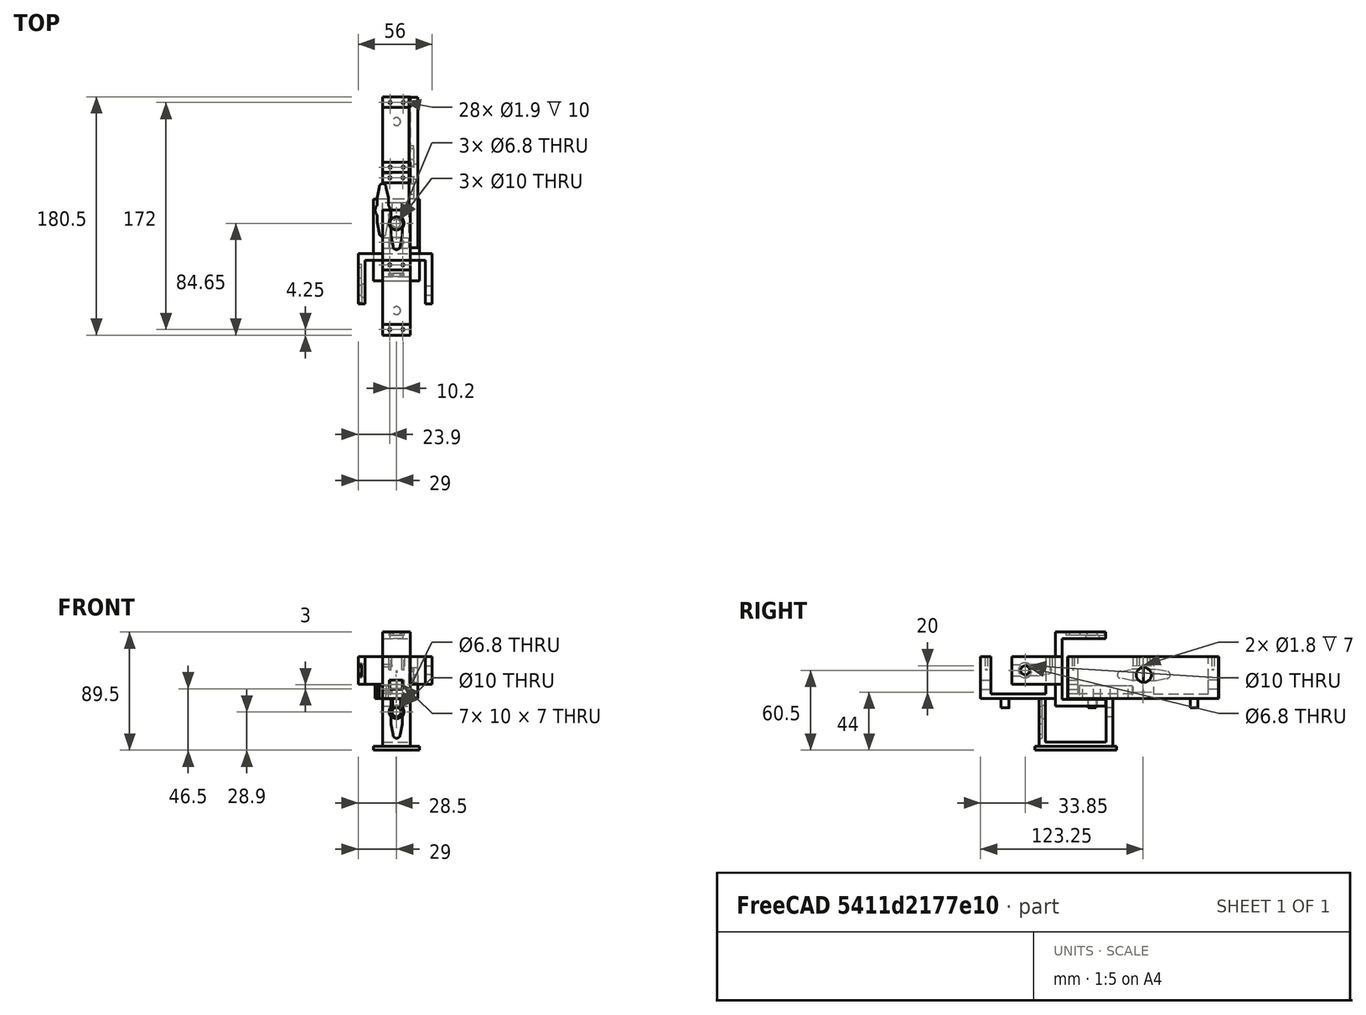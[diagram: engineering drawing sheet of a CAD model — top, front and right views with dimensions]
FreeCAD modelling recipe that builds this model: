
FCSTD DOCUMENT  (FreeCAD 1.0R39109 (Git))
Label: Piernas
License: All rights reserved
LicenseURL: https://en.wikipedia.org/wiki/All_rights_reserved
objects: Part::Cylinder×46, Part::MultiFuse×39, Part::Cut×27, Sketcher::SketchObject×21, PartDesign::Pad×21, PartDesign::Body×21, Part::Box×9, App::DocumentObjectGroup×8, Spreadsheet::Sheet×1, Mesh::Feature×1
note: 247 computed .brp shape members not serialized (recipe doc carries the construction recipe); baked Part::Feature solids carry a one-line shape summary decoded from their .brp

FEATURE [Sketcher::SketchObject] Sketch
  ArcFitTolerance = 0
  AttachmentSupport = -> [YZ_Plane]
  FullyConstrained = true
  MakeInternals = false
  MapMode = 5
  Placement = pos=(0,0,0) rot=(0.57735,0.57735,0.57735;2.0944rad)
  expr: Constraints[10] = Spreadsheet.H_Largo
  expr: Constraints[12] = Spreadsheet.H_BaseAlto
  expr: Constraints[13] = Spreadsheet.H_AltoServo
  expr: Constraints[14] = Spreadsheet.H_AnchoAgg
  sketch-geometry (8):
    g0: LineSegment StartX=-28.75 StartY=32 StartZ=0 EndX=-28.75 EndY=0 EndZ=0
    g1: LineSegment StartX=-28.75 StartY=0 StartZ=0 EndX=28.75 EndY=0 EndZ=0
    g2: LineSegment StartX=28.75 StartY=0 StartZ=0 EndX=28.75 EndY=32 EndZ=0
    g3: LineSegment StartX=28.75 StartY=32 StartZ=0 EndX=20.75 EndY=32 EndZ=0
    g4: LineSegment StartX=20.75 StartY=32 StartZ=0 EndX=20.75 EndY=3.5 EndZ=0
    g5: LineSegment StartX=20.75 StartY=3.5 StartZ=0 EndX=-20.75 EndY=3.5 EndZ=0
    g6: LineSegment StartX=-20.75 StartY=3.5 StartZ=0 EndX=-20.75 EndY=32 EndZ=0
    g7: LineSegment StartX=-28.75 StartY=32 StartZ=0 EndX=-20.75 EndY=32 EndZ=0
  constraints (21):
    c: Coincident(g1,g0)
    c: Coincident(g2,g1)
    c: Vertical(g2)
    c: Coincident(g3,g2)
    c: Coincident(g4,g3)
    c: Vertical(g4)
    c: Coincident(g5,g4)
    c: Horizontal(g5)
    c: Coincident(g6,g5)
    c: Vertical(g6)
    c: DistanceX(g5,g5) = 41.5
    c: Symmetric(g6,g3,g-2)
    c: DistanceY(g0,g5) = 3.5
    c: DistanceY(g4,g4) = 28.5
    c: DistanceX(g3,g3) = 8
    c: Symmetric(g1,g0,g-2)
    c: Symmetric(g0,g2,g-2)
    c: Coincident(g7,g0)
    c: Coincident(g7,g6)
    c: Horizontal(g7)
    c: PointOnObject(g0,g-1)
FEATURE [Spreadsheet::Sheet] Spreadsheet
  cells = A1='HOLDER SERVO; D1='UNION SERVOS; G1='PIE; A2='largo; B2(H_Largo)=41.5; D2='separacion entre servos; E2(U_sepa)=0.5; G2='Largo; H2(P_largo)=62; A3='BaseAlto; B3(H_BaseAlto)=3.5; D3='Grosor Paredes; E3(U_Grosor)=5; G3='Ancho; H3(P_acnho)=35; A4='Alto Servo; B4(H_AltoServo)=28.5; D4='LargoMedio-Sal; E4(U_LargoM)=33; A5='Ancho Aggraderas; B5(H_AnchoAgg)=8; D5='AltoBase-Techo; E5(U_AltoB)=45.5; A6='Ancho Base; B6(H_AnchoBase)=21; A7='Distanciatonillos; B7(H_DistanciaTornillos)=8; A8='RadioTornillos; B8(H_RadioTornillos)==2.3 / 2 - 0.2; A9='Radio eje; B9(H_RadioEje)=3
FEATURE [PartDesign::Pad] Pad
  Direction = (1,-2e-16,3e-16)
  Length = 21
  Length2 = 10
  Placement = pos=(0,0,0) rot=(0.57735,0.57735,0.57735;2.0944rad)
  Profile = -> Sketch
  ReferenceAxis = -> Sketch [N_Axis]
  Suppressed = false
  Type = 0
  expr: Length = Spreadsheet.H_AnchoBase
FEATURE [PartDesign::Body] Body  label="ServoHolder"
  AllowCompound = false
  Group = -> [Sketch,Pad]
  Origin = -> Origin
  Tip = -> Pad
FEATURE [Part::Box] Box  label="Cube"
  AttacherType = Attacher::AttachEngine3D
  Height = 7
  Length = 10
  Placement = pos=(5,-29,4) rot=(0,0,1;0rad)
  Width = 10
FEATURE [Part::Cut] Cut
  Base = -> Body
  Tool = -> Box
FEATURE [Part::Cylinder] Cylinder
  Angle = 360
  AttacherType = Attacher::AttachEngine3D
  FirstAngle = 0
  Height = 10
  Placement = pos=(9.9,0,0) rot=(0,0,1;0rad)
  Radius = 0.95
  SecondAngle = 0
  expr: .Placement.Base.x = Spreadsheet.H_RadioTornillos * 2 + Spreadsheet.H_DistanciaTornillos
  expr: Radius = Spreadsheet.H_RadioTornillos
FEATURE [Part::Cylinder] Cylinder001
  Angle = 360
  AttacherType = Attacher::AttachEngine3D
  FirstAngle = 0
  Height = 10
  Radius = 0.95
  SecondAngle = 0
  expr: Radius = Spreadsheet.H_RadioTornillos
FEATURE [Part::MultiFuse] Fusion  label="Tornillos"
  Placement = pos=(5,24.5,22) rot=(0,0,1;0rad)
  Shapes = -> [Cylinder001,Cylinder]
FEATURE [Part::Cylinder] Cylinder002
  Angle = 360
  AttacherType = Attacher::AttachEngine3D
  FirstAngle = 0
  Height = 10
  Placement = pos=(9.9,0,0) rot=(0,0,1;0rad)
  Radius = 0.95
  SecondAngle = 0
  expr: .Placement.Base.x = Spreadsheet.H_RadioTornillos * 2 + Spreadsheet.H_DistanciaTornillos
  expr: Radius = Spreadsheet.H_RadioTornillos
FEATURE [Part::Cylinder] Cylinder003
  Angle = 360
  AttacherType = Attacher::AttachEngine3D
  FirstAngle = 0
  Height = 10
  Radius = 0.95
  SecondAngle = 0
  expr: Radius = Spreadsheet.H_RadioTornillos
FEATURE [Part::MultiFuse] Fusion001  label="Tornillos001"
  Placement = pos=(5,-24.5,22) rot=(0,0,1;0rad)
  Shapes = -> [Cylinder003,Cylinder002]
FEATURE [Part::MultiFuse] Fusion002
  Placement = pos=(0.4,0,0) rot=(0,0,1;0rad)
  Shapes = -> [Fusion,Fusion001]
FEATURE [Part::Cut] Cut001  label="Holder001"
  Base = -> Cut
  Tool = -> Fusion002
FEATURE [Part::Cylinder] Cylinder012
  Angle = 360
  AttacherType = Attacher::AttachEngine3D
  FirstAngle = 0
  Height = 10
  Placement = pos=(10.5,-10.1,-7) rot=(0,0,1;0rad)
  Radius = 3
  SecondAngle = 0
  expr: Radius = Spreadsheet.H_RadioEje
FEATURE [Part::Box] Box003  label="Cube003"
  AttacherType = Attacher::AttachEngine3D
  Height = 7
  Length = 10
  Placement = pos=(5,-29,7) rot=(0,0,1;0rad)
  Width = 10
FEATURE [Part::Cylinder] Cylinder013
  Angle = 360
  AttacherType = Attacher::AttachEngine3D
  FirstAngle = 0
  Height = 10
  Placement = pos=(9.9,0,0) rot=(0,0,1;0rad)
  Radius = 0.95
  SecondAngle = 0
  expr: .Placement.Base.x = Spreadsheet.H_RadioTornillos * 2 + Spreadsheet.H_DistanciaTornillos
  expr: Radius = Spreadsheet.H_RadioTornillos
FEATURE [Part::Cylinder] Cylinder014
  Angle = 360
  AttacherType = Attacher::AttachEngine3D
  FirstAngle = 0
  Height = 10
  Radius = 0.95
  SecondAngle = 0
  expr: Radius = Spreadsheet.H_RadioTornillos
FEATURE [Part::Cylinder] Cylinder015
  Angle = 360
  AttacherType = Attacher::AttachEngine3D
  FirstAngle = 0
  Height = 10
  Placement = pos=(9.9,0,0) rot=(0,0,1;0rad)
  Radius = 0.95
  SecondAngle = 0
  expr: .Placement.Base.x = Spreadsheet.H_RadioTornillos * 2 + Spreadsheet.H_DistanciaTornillos
  expr: Radius = Spreadsheet.H_RadioTornillos
FEATURE [Part::Cylinder] Cylinder016
  Angle = 360
  AttacherType = Attacher::AttachEngine3D
  FirstAngle = 0
  Height = 10
  Radius = 0.95
  SecondAngle = 0
  expr: Radius = Spreadsheet.H_RadioTornillos
FEATURE [Part::MultiFuse] Fusion010  label="Tornillos006"
  Placement = pos=(5,24.5,22) rot=(0,0,1;0rad)
  Shapes = -> [Cylinder014,Cylinder013]
FEATURE [Part::MultiFuse] Fusion011  label="Tornillos007"
  Placement = pos=(5,-24.5,22) rot=(0,0,1;0rad)
  Shapes = -> [Cylinder016,Cylinder015]
FEATURE [Part::MultiFuse] Fusion012
  Placement = pos=(0.4,0,0) rot=(0,0,1;0rad)
  Shapes = -> [Fusion010,Fusion011]
FEATURE [Sketcher::SketchObject] Sketch003
  ArcFitTolerance = 0
  AttachmentSupport = -> [YZ_Plane003]
  FullyConstrained = true
  MakeInternals = false
  MapMode = 5
  Placement = pos=(0,0,0) rot=(0.57735,0.57735,0.57735;2.0944rad)
  expr: Constraints[10] = Spreadsheet.H_Largo
  expr: Constraints[12] = Spreadsheet.H_BaseAlto
  expr: Constraints[13] = Spreadsheet.H_AltoServo
  expr: Constraints[14] = Spreadsheet.H_AnchoAgg
  sketch-geometry (8):
    g0: LineSegment StartX=-28.75 StartY=32 StartZ=0 EndX=-28.75 EndY=0 EndZ=0
    g1: LineSegment StartX=-28.75 StartY=0 StartZ=0 EndX=28.75 EndY=0 EndZ=0
    g2: LineSegment StartX=28.75 StartY=0 StartZ=0 EndX=28.75 EndY=32 EndZ=0
    g3: LineSegment StartX=28.75 StartY=32 StartZ=0 EndX=20.75 EndY=32 EndZ=0
    g4: LineSegment StartX=20.75 StartY=32 StartZ=0 EndX=20.75 EndY=3.5 EndZ=0
    g5: LineSegment StartX=20.75 StartY=3.5 StartZ=0 EndX=-20.75 EndY=3.5 EndZ=0
    g6: LineSegment StartX=-20.75 StartY=3.5 StartZ=0 EndX=-20.75 EndY=32 EndZ=0
    g7: LineSegment StartX=-28.75 StartY=32 StartZ=0 EndX=-20.75 EndY=32 EndZ=0
  constraints (21):
    c: Coincident(g1,g0)
    c: Coincident(g2,g1)
    c: Vertical(g2)
    c: Coincident(g3,g2)
    c: Coincident(g4,g3)
    c: Vertical(g4)
    c: Coincident(g5,g4)
    c: Horizontal(g5)
    c: Coincident(g6,g5)
    c: Vertical(g6)
    c: DistanceX(g5,g5) = 41.5
    c: Symmetric(g6,g3,g-2)
    c: DistanceY(g0,g5) = 3.5
    c: DistanceY(g4,g4) = 28.5
    c: DistanceX(g3,g3) = 8
    c: Symmetric(g1,g0,g-2)
    c: Symmetric(g0,g2,g-2)
    c: Coincident(g7,g0)
    c: Coincident(g7,g6)
    c: Horizontal(g7)
    c: PointOnObject(g0,g-1)
FEATURE [PartDesign::Pad] Pad003
  Direction = (1,-2e-16,3e-16)
  Length = 21
  Length2 = 10
  Placement = pos=(0,0,0) rot=(0.57735,0.57735,0.57735;2.0944rad)
  Profile = -> Sketch003
  ReferenceAxis = -> Sketch003 [N_Axis]
  Suppressed = false
  Type = 0
  expr: Length = Spreadsheet.H_AnchoBase
FEATURE [PartDesign::Body] Body003  label="ServoHolder003"
  AllowCompound = false
  Group = -> [Sketch003,Pad003]
  Origin = -> Origin003
  Tip = -> Pad003
FEATURE [Part::Cut] Cut006
  Base = -> Body003
  Tool = -> Box003
FEATURE [Part::Cut] Cut007  label="Holder004"
  Base = -> Cut006
  Tool = -> Fusion012
FEATURE [Part::MultiFuse] Fusion013  label="HolderCEje"
  Shapes = -> [Cylinder012,Cut007]
FEATURE [App::DocumentObjectGroup] Group  label="Muslo2"
  Group = -> [Cut001,Fusion013]
FEATURE [Sketcher::SketchObject] Sketch004
  ArcFitTolerance = 0
  AttachmentSupport = -> [YZ_Plane004]
  FullyConstrained = true
  MakeInternals = false
  MapMode = 5
  Placement = pos=(0,0,0) rot=(0.57735,0.57735,0.57735;2.0944rad)
  expr: Constraints[16] = Spreadsheet.U_sepa
  expr: Constraints[17] = Spreadsheet.U_LargoM
  expr: Constraints[20] = Spreadsheet.U_Grosor
  expr: Constraints[21] = Spreadsheet.U_Grosor
  expr: Constraints[22] = Spreadsheet.U_Grosor
  expr: Constraints[23] = Spreadsheet.U_AltoB
  sketch-geometry (8):
    g0: LineSegment StartX=-33 StartY=-0.5 StartZ=0 EndX=0 EndY=-0.5 EndZ=0
    g1: LineSegment StartX=0 StartY=-0.5 StartZ=0 EndX=0 EndY=-5.5 EndZ=0
    g2: LineSegment StartX=0 StartY=-5.5 StartZ=0 EndX=-38 EndY=-5.5 EndZ=0
    g3: LineSegment StartX=-38 StartY=-5.5 StartZ=0 EndX=-38 EndY=50.5 EndZ=0
    g4: LineSegment StartX=-38 StartY=50.5 StartZ=0 EndX=0 EndY=50.5 EndZ=0
    g5: LineSegment StartX=0 StartY=50.5 StartZ=0 EndX=0 EndY=45.5 EndZ=0
    g6: LineSegment StartX=0 StartY=45.5 StartZ=0 EndX=-33 EndY=45.5 EndZ=0
    g7: LineSegment StartX=-33 StartY=45.5 StartZ=0 EndX=-33 EndY=-0.5 EndZ=0
  constraints (24):
    c: Horizontal(g0)
    c: Coincident(g1,g0)
    c: Vertical(g1)
    c: Coincident(g2,g1)
    c: Horizontal(g2)
    c: Coincident(g3,g2)
    c: Vertical(g3)
    c: Coincident(g4,g3)
    c: Horizontal(g4)
    c: Coincident(g5,g4)
    c: Vertical(g5)
    c: Coincident(g6,g5)
    c: Horizontal(g6)
    c: Coincident(g7,g6)
    c: Coincident(g7,g0)
    c: Vertical(g7)
    c: DistanceY(g0,g-1) = 0.5
    c: DistanceX(g0,g-1) = 33
    c: PointOnObject(g0,g-2)
    c: PointOnObject(g5,g-2)
    c: DistanceX(g3,g6) = 5
    c: DistanceY(g5,g4) = 5
    c: DistanceY(g1,g1) = 5
    c: DistanceY(g-1,g5) = 45.5
FEATURE [PartDesign::Pad] Pad004
  Direction = (1,-2e-16,3e-16)
  Length = 21
  Length2 = 10
  Placement = pos=(0,0,0) rot=(0.57735,0.57735,0.57735;2.0944rad)
  Profile = -> Sketch004
  ReferenceAxis = -> Sketch004 [N_Axis]
  Suppressed = false
  Type = 0
  expr: Length = Spreadsheet.H_AnchoBase
FEATURE [PartDesign::Body] Body004  label="U"
  AllowCompound = false
  Group = -> [Sketch004,Pad004]
  Origin = -> Origin004
  Tip = -> Pad004
FEATURE [Sketcher::SketchObject] Sketch005
  ArcFitTolerance = 0
  AttachmentSupport = -> [XY_Plane005]
  FullyConstrained = true
  MakeInternals = false
  MapMode = 5
  sketch-geometry (13):
    g0: LineSegment StartX=-4.25 StartY=3.75 StartZ=0 EndX=-4.25 EndY=9.25 EndZ=0
    g1: LineSegment StartX=4.25 StartY=3.75 StartZ=0 EndX=4.25 EndY=9.25 EndZ=0
    g2: LineSegment StartX=-4.25 StartY=-3.75 StartZ=0 EndX=-4.25 EndY=-9.25 EndZ=0
    g3: LineSegment StartX=4.25 StartY=-3.75 StartZ=0 EndX=4.25 EndY=-9.25 EndZ=0
    g4: LineSegment StartX=-4.25 StartY=9.25 StartZ=0 EndX=-2.65 EndY=17.2924 EndZ=0
    g5: LineSegment StartX=2.65 StartY=17.2924 StartZ=0 EndX=4.25 EndY=9.25 EndZ=0
    g6: LineSegment StartX=-4.25 StartY=-9.25 StartZ=0 EndX=-2.65 EndY=-17.2924 EndZ=0
    g7: LineSegment StartX=2.65 StartY=-17.2924 StartZ=0 EndX=4.25 EndY=-9.25 EndZ=0
    g8: GeomPoint [constr] X=0 Y=20 Z=0
    g9: ArcOfCircle CenterX=-1e-16 CenterY=17.3494 CenterZ=0 NormalX=0 NormalY=0 NormalZ=1 AngleXU=0 Radius=2.65061 StartAngle=6.26168 EndAngle=9.44628
    g10: ArcOfCircle CenterX=0.0427264 CenterY=-1e-16 CenterZ=0 NormalX=0 NormalY=0 NormalZ=1 AngleXU=0 Radius=5.7 StartAngle=2.42357 EndAngle=3.85961
    g11: ArcOfCircle CenterX=-0.0427264 CenterY=0 CenterZ=0 NormalX=0 NormalY=0 NormalZ=1 AngleXU=0 Radius=5.7 StartAngle=5.56517 EndAngle=7.00121
    g12: ArcOfCircle CenterX=2e-16 CenterY=-17.3494 CenterZ=0 NormalX=0 NormalY=0 NormalZ=1 AngleXU=0 Radius=2.65061 StartAngle=3.12009 EndAngle=6.30469
  constraints (36):
    c: Vertical(g0)
    c: Vertical(g1)
    c: Vertical(g2)
    c: Vertical(g3)
    c: Symmetric(g0,g1,g-2)
    c: Symmetric(g0,g2,g-1)
    c: Symmetric(g2,g3,g-2)
    c: Equal(g1,g0)
    c: Equal(g2,g3)
    c: Equal(g2,g0)
    c: Coincident(g4,g0)
    c: Coincident(g5,g1)
    c: Coincident(g6,g2)
    c: Coincident(g7,g3)
    c: Symmetric(g4,g5,g-2)
    c: Symmetric(g6,g7,g-2)
    c: Symmetric(g4,g6,g-1)
    c: DistanceY(g0,g0) = 5.5
    c: PointOnObject(g8,g-2)
    c: DistanceY(g-1,g8) = 20
    c: Coincident(g9,g4)
    c: Coincident(g9,g5)
    c: Distance(g4) = 8.2
    c: Coincident(g10,g0)
    c: Coincident(g10,g2)
    c: Coincident(g11,g1)
    c: Coincident(g11,g3)
    c: Coincident(g12,g6)
    c: Coincident(g12,g7)
    c: PointOnObject(g8,g9)
    c: DistanceX(g4,g5) = 5.3
    c: Symmetric(g9,g12,g-1)
    c: DistanceY(g2,g0) = 7.5
    c: DistanceX(g0,g1) = 8.5
    c: Radius(g11) = 5.7
    c: Equal(g10,g11)
FEATURE [PartDesign::Pad] Pad005
  Direction = (0,0,1)
  Length = 10
  Length2 = 10
  Profile = -> Sketch005
  ReferenceAxis = -> Sketch005 [N_Axis]
  Suppressed = false
  Type = 0
FEATURE [PartDesign::Body] Body005  label="Lever"
  AllowCompound = false
  Group = -> [Sketch005,Pad005]
  Origin = -> Origin005
  Tip = -> Pad005
FEATURE [Mesh::Feature] MG995
  Placement = pos=(27.6,-7,6) rot=(0,0,1;3.14159rad)
FEATURE [Sketcher::SketchObject] Sketch006
  ArcFitTolerance = 0
  AttachmentSupport = -> [XY_Plane005]
  FullyConstrained = true
  MakeInternals = false
  MapMode = 5
  sketch-geometry (13):
    g0: LineSegment StartX=-4.25 StartY=3.75 StartZ=0 EndX=-4.25 EndY=9.25 EndZ=0
    g1: LineSegment StartX=4.25 StartY=3.75 StartZ=0 EndX=4.25 EndY=9.25 EndZ=0
    g2: LineSegment StartX=-4.25 StartY=-3.75 StartZ=0 EndX=-4.25 EndY=-9.25 EndZ=0
    g3: LineSegment StartX=4.25 StartY=-3.75 StartZ=0 EndX=4.25 EndY=-9.25 EndZ=0
    g4: LineSegment StartX=-4.25 StartY=9.25 StartZ=0 EndX=-2.65 EndY=17.2924 EndZ=0
    g5: LineSegment StartX=2.65 StartY=17.2924 StartZ=0 EndX=4.25 EndY=9.25 EndZ=0
    g6: LineSegment StartX=-4.25 StartY=-9.25 StartZ=0 EndX=-2.65 EndY=-17.2924 EndZ=0
    g7: LineSegment StartX=2.65 StartY=-17.2924 StartZ=0 EndX=4.25 EndY=-9.25 EndZ=0
    g8: GeomPoint [constr] X=0 Y=20 Z=0
    g9: ArcOfCircle CenterX=-1e-16 CenterY=17.3494 CenterZ=0 NormalX=0 NormalY=0 NormalZ=1 AngleXU=0 Radius=2.65061 StartAngle=6.26168 EndAngle=9.44628
    g10: ArcOfCircle CenterX=0.0427264 CenterY=-1e-16 CenterZ=0 NormalX=0 NormalY=0 NormalZ=1 AngleXU=0 Radius=5.7 StartAngle=2.42357 EndAngle=3.85961
    g11: ArcOfCircle CenterX=-0.0427264 CenterY=0 CenterZ=0 NormalX=0 NormalY=0 NormalZ=1 AngleXU=0 Radius=5.7 StartAngle=5.56517 EndAngle=7.00121
    g12: ArcOfCircle CenterX=2e-16 CenterY=-17.3494 CenterZ=0 NormalX=0 NormalY=0 NormalZ=1 AngleXU=0 Radius=2.65061 StartAngle=3.12009 EndAngle=6.30469
  constraints (36):
    c: Vertical(g0)
    c: Vertical(g1)
    c: Vertical(g2)
    c: Vertical(g3)
    c: Symmetric(g0,g1,g-2)
    c: Symmetric(g0,g2,g-1)
    c: Symmetric(g2,g3,g-2)
    c: Equal(g1,g0)
    c: Equal(g2,g3)
    c: Equal(g2,g0)
    c: Coincident(g4,g0)
    c: Coincident(g5,g1)
    c: Coincident(g6,g2)
    c: Coincident(g7,g3)
    c: Symmetric(g4,g5,g-2)
    c: Symmetric(g6,g7,g-2)
    c: Symmetric(g4,g6,g-1)
    c: DistanceY(g0,g0) = 5.5
    c: PointOnObject(g8,g-2)
    c: DistanceY(g-1,g8) = 20
    c: Coincident(g9,g4)
    c: Coincident(g9,g5)
    c: Distance(g4) = 8.2
    c: Coincident(g10,g0)
    c: Coincident(g10,g2)
    c: Coincident(g11,g1)
    c: Coincident(g11,g3)
    c: Coincident(g12,g6)
    c: Coincident(g12,g7)
    c: PointOnObject(g8,g9)
    c: DistanceX(g4,g5) = 5.3
    c: Symmetric(g9,g12,g-1)
    c: DistanceY(g2,g0) = 7.5
    c: DistanceX(g0,g1) = 8.5
    c: Radius(g11) = 5.7
    c: Equal(g10,g11)
FEATURE [PartDesign::Pad] Pad006
  Direction = (0,0,1)
  Length = 5
  Length2 = 10
  Profile = -> Sketch006
  ReferenceAxis = -> Sketch006 [N_Axis]
  Suppressed = false
  Type = 0
FEATURE [PartDesign::Body] Body006  label="Lever001"
  AllowCompound = false
  Group = -> [Sketch006,Pad006]
  Origin = -> Origin006
  Placement = pos=(10.5,-10,48) rot=(0,0,1;0rad)
  Tip = -> Pad006
FEATURE [Part::Cylinder] Cylinder017
  Angle = 360
  AttacherType = Attacher::AttachEngine3D
  FirstAngle = 0
  Height = 9
  Placement = pos=(10.5,-10.1,44) rot=(0,0,1;0rad)
  Radius = 5
  SecondAngle = 0
  expr: Radius = 5
FEATURE [App::DocumentObjectGroup] Group004  label="workbecnh"
FEATURE [Part::MultiFuse] Fusion014
  Shapes = -> [Body006,Cylinder017]
FEATURE [Part::Cut] Cut008
  Base = -> Body004
  Tool = -> Fusion014
FEATURE [Part::Cylinder] Cylinder018
  Angle = 360
  AttacherType = Attacher::AttachEngine3D
  FirstAngle = 0
  Height = 44
  Placement = pos=(10.5,-10.1,-9) rot=(0,0,1;0rad)
  Radius = 3.4
  SecondAngle = 0
  expr: Radius = Spreadsheet.H_RadioEje + 0.4
FEATURE [Part::Cut] Cut009  label="Agarre"
  Base = -> Cut008
  Tool = -> Cylinder018
FEATURE [App::DocumentObjectGroup] Group002  label="UTILS"
  Group = -> [MG995,Body005,Cut009]
FEATURE [Part::Box] Box004  label="Cube004"
  AttacherType = Attacher::AttachEngine3D
  Height = 7
  Length = 10
  Placement = pos=(5,-29,7) rot=(0,0,1;0rad)
  Width = 10
FEATURE [Part::Cylinder] Cylinder019
  Angle = 360
  AttacherType = Attacher::AttachEngine3D
  FirstAngle = 0
  Height = 10
  Placement = pos=(10.5,-10.1,-7) rot=(0,0,1;0rad)
  Radius = 3
  SecondAngle = 0
  expr: Radius = Spreadsheet.H_RadioEje
FEATURE [Part::Cylinder] Cylinder020
  Angle = 360
  AttacherType = Attacher::AttachEngine3D
  FirstAngle = 0
  Height = 10
  Placement = pos=(9.9,0,0) rot=(0,0,1;0rad)
  Radius = 0.95
  SecondAngle = 0
  expr: .Placement.Base.x = Spreadsheet.H_RadioTornillos * 2 + Spreadsheet.H_DistanciaTornillos
  expr: Radius = Spreadsheet.H_RadioTornillos
FEATURE [Part::Cylinder] Cylinder021
  Angle = 360
  AttacherType = Attacher::AttachEngine3D
  FirstAngle = 0
  Height = 10
  Radius = 0.95
  SecondAngle = 0
  expr: Radius = Spreadsheet.H_RadioTornillos
FEATURE [Part::Cylinder] Cylinder022
  Angle = 360
  AttacherType = Attacher::AttachEngine3D
  FirstAngle = 0
  Height = 10
  Placement = pos=(9.9,0,0) rot=(0,0,1;0rad)
  Radius = 0.95
  SecondAngle = 0
  expr: .Placement.Base.x = Spreadsheet.H_RadioTornillos * 2 + Spreadsheet.H_DistanciaTornillos
  expr: Radius = Spreadsheet.H_RadioTornillos
FEATURE [Part::Cylinder] Cylinder023
  Angle = 360
  AttacherType = Attacher::AttachEngine3D
  FirstAngle = 0
  Height = 10
  Radius = 0.95
  SecondAngle = 0
  expr: Radius = Spreadsheet.H_RadioTornillos
FEATURE [Part::MultiFuse] Fusion015  label="Tornillos008"
  Placement = pos=(5,24.5,22) rot=(0,0,1;0rad)
  Shapes = -> [Cylinder021,Cylinder020]
FEATURE [Part::MultiFuse] Fusion016  label="Tornillos009"
  Placement = pos=(5,-24.5,22) rot=(0,0,1;0rad)
  Shapes = -> [Cylinder023,Cylinder022]
FEATURE [Part::MultiFuse] Fusion017
  Placement = pos=(0.4,0,0) rot=(0,0,1;0rad)
  Shapes = -> [Fusion015,Fusion016]
FEATURE [Sketcher::SketchObject] Sketch007
  ArcFitTolerance = 0
  AttachmentSupport = -> [YZ_Plane007]
  FullyConstrained = true
  MakeInternals = false
  MapMode = 5
  Placement = pos=(0,0,0) rot=(0.57735,0.57735,0.57735;2.0944rad)
  expr: Constraints[10] = Spreadsheet.H_Largo
  expr: Constraints[12] = Spreadsheet.H_BaseAlto
  expr: Constraints[13] = Spreadsheet.H_AltoServo
  expr: Constraints[14] = Spreadsheet.H_AnchoAgg
  sketch-geometry (8):
    g0: LineSegment StartX=-28.75 StartY=32 StartZ=0 EndX=-28.75 EndY=0 EndZ=0
    g1: LineSegment StartX=-28.75 StartY=0 StartZ=0 EndX=28.75 EndY=0 EndZ=0
    g2: LineSegment StartX=28.75 StartY=0 StartZ=0 EndX=28.75 EndY=32 EndZ=0
    g3: LineSegment StartX=28.75 StartY=32 StartZ=0 EndX=20.75 EndY=32 EndZ=0
    g4: LineSegment StartX=20.75 StartY=32 StartZ=0 EndX=20.75 EndY=3.5 EndZ=0
    g5: LineSegment StartX=20.75 StartY=3.5 StartZ=0 EndX=-20.75 EndY=3.5 EndZ=0
    g6: LineSegment StartX=-20.75 StartY=3.5 StartZ=0 EndX=-20.75 EndY=32 EndZ=0
    g7: LineSegment StartX=-28.75 StartY=32 StartZ=0 EndX=-20.75 EndY=32 EndZ=0
  constraints (21):
    c: Coincident(g1,g0)
    c: Coincident(g2,g1)
    c: Vertical(g2)
    c: Coincident(g3,g2)
    c: Coincident(g4,g3)
    c: Vertical(g4)
    c: Coincident(g5,g4)
    c: Horizontal(g5)
    c: Coincident(g6,g5)
    c: Vertical(g6)
    c: DistanceX(g5,g5) = 41.5
    c: Symmetric(g6,g3,g-2)
    c: DistanceY(g0,g5) = 3.5
    c: DistanceY(g4,g4) = 28.5
    c: DistanceX(g3,g3) = 8
    c: Symmetric(g1,g0,g-2)
    c: Symmetric(g0,g2,g-2)
    c: Coincident(g7,g0)
    c: Coincident(g7,g6)
    c: Horizontal(g7)
    c: PointOnObject(g0,g-1)
FEATURE [PartDesign::Pad] Pad007
  Direction = (1,-2e-16,3e-16)
  Length = 21
  Length2 = 10
  Placement = pos=(0,0,0) rot=(0.57735,0.57735,0.57735;2.0944rad)
  Profile = -> Sketch007
  ReferenceAxis = -> Sketch007 [N_Axis]
  Suppressed = false
  Type = 0
  expr: Length = Spreadsheet.H_AnchoBase
FEATURE [PartDesign::Body] Body007  label="ServoHolder004"
  AllowCompound = false
  Group = -> [Sketch007,Pad007]
  Origin = -> Origin007
  Tip = -> Pad007
FEATURE [Part::Cut] Cut010
  Base = -> Body007
  Tool = -> Box004
FEATURE [Part::Cut] Cut011  label="Holder005"
  Base = -> Cut010
  Tool = -> Fusion017
FEATURE [Part::MultiFuse] Fusion018  label="HolderCEje001"
  Shapes = -> [Cylinder019,Cut011]
FEATURE [Part::Box] Box005  label="Cube005"
  AttacherType = Attacher::AttachEngine3D
  Height = 7
  Length = 10
  Placement = pos=(5,-29,7) rot=(0,0,1;0rad)
  Width = 10
FEATURE [Part::Cylinder] Cylinder024
  Angle = 360
  AttacherType = Attacher::AttachEngine3D
  FirstAngle = 0
  Height = 10
  Placement = pos=(10.5,-10.1,-7) rot=(0,0,1;0rad)
  Radius = 3
  SecondAngle = 0
  expr: Radius = Spreadsheet.H_RadioEje
FEATURE [Part::Cylinder] Cylinder025
  Angle = 360
  AttacherType = Attacher::AttachEngine3D
  FirstAngle = 0
  Height = 10
  Placement = pos=(9.9,0,0) rot=(0,0,1;0rad)
  Radius = 0.95
  SecondAngle = 0
  expr: .Placement.Base.x = Spreadsheet.H_RadioTornillos * 2 + Spreadsheet.H_DistanciaTornillos
  expr: Radius = Spreadsheet.H_RadioTornillos
FEATURE [Part::Cylinder] Cylinder026
  Angle = 360
  AttacherType = Attacher::AttachEngine3D
  FirstAngle = 0
  Height = 10
  Radius = 0.95
  SecondAngle = 0
  expr: Radius = Spreadsheet.H_RadioTornillos
FEATURE [Part::Cylinder] Cylinder027
  Angle = 360
  AttacherType = Attacher::AttachEngine3D
  FirstAngle = 0
  Height = 10
  Placement = pos=(9.9,0,0) rot=(0,0,1;0rad)
  Radius = 0.95
  SecondAngle = 0
  expr: .Placement.Base.x = Spreadsheet.H_RadioTornillos * 2 + Spreadsheet.H_DistanciaTornillos
  expr: Radius = Spreadsheet.H_RadioTornillos
FEATURE [Part::Cylinder] Cylinder028
  Angle = 360
  AttacherType = Attacher::AttachEngine3D
  FirstAngle = 0
  Height = 10
  Radius = 0.95
  SecondAngle = 0
  expr: Radius = Spreadsheet.H_RadioTornillos
FEATURE [Part::MultiFuse] Fusion019  label="Tornillos010"
  Placement = pos=(5,24.5,22) rot=(0,0,1;0rad)
  Shapes = -> [Cylinder026,Cylinder025]
FEATURE [Part::MultiFuse] Fusion020  label="Tornillos011"
  Placement = pos=(5,-24.5,22) rot=(0,0,1;0rad)
  Shapes = -> [Cylinder028,Cylinder027]
FEATURE [Part::MultiFuse] Fusion021
  Placement = pos=(0.4,0,0) rot=(0,0,1;0rad)
  Shapes = -> [Fusion019,Fusion020]
FEATURE [Sketcher::SketchObject] Sketch008
  ArcFitTolerance = 0
  AttachmentSupport = -> [YZ_Plane008]
  FullyConstrained = true
  MakeInternals = false
  MapMode = 5
  Placement = pos=(0,0,0) rot=(0.57735,0.57735,0.57735;2.0944rad)
  expr: Constraints[10] = Spreadsheet.H_Largo
  expr: Constraints[12] = Spreadsheet.H_BaseAlto
  expr: Constraints[13] = Spreadsheet.H_AltoServo
  expr: Constraints[14] = Spreadsheet.H_AnchoAgg
  sketch-geometry (8):
    g0: LineSegment StartX=-28.75 StartY=32 StartZ=0 EndX=-28.75 EndY=0 EndZ=0
    g1: LineSegment StartX=-28.75 StartY=0 StartZ=0 EndX=28.75 EndY=0 EndZ=0
    g2: LineSegment StartX=28.75 StartY=0 StartZ=0 EndX=28.75 EndY=32 EndZ=0
    g3: LineSegment StartX=28.75 StartY=32 StartZ=0 EndX=20.75 EndY=32 EndZ=0
    g4: LineSegment StartX=20.75 StartY=32 StartZ=0 EndX=20.75 EndY=3.5 EndZ=0
    g5: LineSegment StartX=20.75 StartY=3.5 StartZ=0 EndX=-20.75 EndY=3.5 EndZ=0
    g6: LineSegment StartX=-20.75 StartY=3.5 StartZ=0 EndX=-20.75 EndY=32 EndZ=0
    g7: LineSegment StartX=-28.75 StartY=32 StartZ=0 EndX=-20.75 EndY=32 EndZ=0
  constraints (21):
    c: Coincident(g1,g0)
    c: Coincident(g2,g1)
    c: Vertical(g2)
    c: Coincident(g3,g2)
    c: Coincident(g4,g3)
    c: Vertical(g4)
    c: Coincident(g5,g4)
    c: Horizontal(g5)
    c: Coincident(g6,g5)
    c: Vertical(g6)
    c: DistanceX(g5,g5) = 41.5
    c: Symmetric(g6,g3,g-2)
    c: DistanceY(g0,g5) = 3.5
    c: DistanceY(g4,g4) = 28.5
    c: DistanceX(g3,g3) = 8
    c: Symmetric(g1,g0,g-2)
    c: Symmetric(g0,g2,g-2)
    c: Coincident(g7,g0)
    c: Coincident(g7,g6)
    c: Horizontal(g7)
    c: PointOnObject(g0,g-1)
FEATURE [PartDesign::Pad] Pad008
  Direction = (1,-2e-16,3e-16)
  Length = 21
  Length2 = 10
  Placement = pos=(0,0,0) rot=(0.57735,0.57735,0.57735;2.0944rad)
  Profile = -> Sketch008
  ReferenceAxis = -> Sketch008 [N_Axis]
  Suppressed = false
  Type = 0
  expr: Length = Spreadsheet.H_AnchoBase
FEATURE [PartDesign::Body] Body008  label="ServoHolder005"
  AllowCompound = false
  Group = -> [Sketch008,Pad008]
  Origin = -> Origin008
  Tip = -> Pad008
FEATURE [Part::Cut] Cut012
  Base = -> Body008
  Tool = -> Box005
FEATURE [Part::Cut] Cut013  label="Holder006"
  Base = -> Cut012
  Tool = -> Fusion021
FEATURE [Part::MultiFuse] Fusion022  label="HolderCEje002"
  Placement = pos=(21,57,0) rot=(0,0,1;3.14159rad)
  Shapes = -> [Cylinder024,Cut013]
FEATURE [Part::MultiFuse] Fusion023
  Shapes = -> [Fusion022,Fusion018]
FEATURE [App::DocumentObjectGroup] Group001  label="Muslo"
  Group = -> [Fusion023]
FEATURE [Part::Cylinder] Cylinder029
  Angle = 360
  AttacherType = Attacher::AttachEngine3D
  FirstAngle = 0
  Height = 9
  Placement = pos=(10.5,-10.1,45) rot=(0,0,1;0rad)
  Radius = 5
  SecondAngle = 0
  expr: Radius = 5
FEATURE [Part::Cylinder] Cylinder030
  Angle = 360
  AttacherType = Attacher::AttachEngine3D
  FirstAngle = 0
  Height = 44
  Placement = pos=(10.5,-10.1,-9) rot=(0,0,1;0rad)
  Radius = 3.4
  SecondAngle = 0
  expr: Radius = Spreadsheet.H_RadioEje + 0.4
FEATURE [Sketcher::SketchObject] Sketch009
  ArcFitTolerance = 0
  AttachmentSupport = -> [YZ_Plane009]
  FullyConstrained = true
  MakeInternals = false
  MapMode = 5
  Placement = pos=(0,0,0) rot=(0.57735,0.57735,0.57735;2.0944rad)
  expr: Constraints[16] = Spreadsheet.U_sepa
  expr: Constraints[17] = Spreadsheet.U_LargoM
  expr: Constraints[20] = Spreadsheet.U_Grosor
  expr: Constraints[21] = Spreadsheet.U_Grosor
  expr: Constraints[22] = Spreadsheet.U_Grosor
  expr: Constraints[23] = Spreadsheet.U_AltoB
  sketch-geometry (8):
    g0: LineSegment StartX=-33 StartY=-0.5 StartZ=0 EndX=0 EndY=-0.5 EndZ=0
    g1: LineSegment StartX=0 StartY=-0.5 StartZ=0 EndX=0 EndY=-5.5 EndZ=0
    g2: LineSegment StartX=0 StartY=-5.5 StartZ=0 EndX=-38 EndY=-5.5 EndZ=0
    g3: LineSegment StartX=-38 StartY=-5.5 StartZ=0 EndX=-38 EndY=50.5 EndZ=0
    g4: LineSegment StartX=-38 StartY=50.5 StartZ=0 EndX=0 EndY=50.5 EndZ=0
    g5: LineSegment StartX=0 StartY=50.5 StartZ=0 EndX=0 EndY=45.5 EndZ=0
    g6: LineSegment StartX=0 StartY=45.5 StartZ=0 EndX=-33 EndY=45.5 EndZ=0
    g7: LineSegment StartX=-33 StartY=45.5 StartZ=0 EndX=-33 EndY=-0.5 EndZ=0
  constraints (24):
    c: Horizontal(g0)
    c: Coincident(g1,g0)
    c: Vertical(g1)
    c: Coincident(g2,g1)
    c: Horizontal(g2)
    c: Coincident(g3,g2)
    c: Vertical(g3)
    c: Coincident(g4,g3)
    c: Horizontal(g4)
    c: Coincident(g5,g4)
    c: Vertical(g5)
    c: Coincident(g6,g5)
    c: Horizontal(g6)
    c: Coincident(g7,g6)
    c: Coincident(g7,g0)
    c: Vertical(g7)
    c: DistanceY(g0,g-1) = 0.5
    c: DistanceX(g0,g-1) = 33
    c: PointOnObject(g0,g-2)
    c: PointOnObject(g5,g-2)
    c: DistanceX(g3,g6) = 5
    c: DistanceY(g5,g4) = 5
    c: DistanceY(g1,g1) = 5
    c: DistanceY(g-1,g5) = 45.5
FEATURE [PartDesign::Pad] Pad009
  Direction = (1,-2e-16,3e-16)
  Length = 21
  Length2 = 10
  Placement = pos=(0,0,0) rot=(0.57735,0.57735,0.57735;2.0944rad)
  Profile = -> Sketch009
  ReferenceAxis = -> Sketch009 [N_Axis]
  Suppressed = false
  Type = 0
  expr: Length = Spreadsheet.H_AnchoBase
FEATURE [PartDesign::Body] Body009  label="U001"
  AllowCompound = false
  Group = -> [Sketch009,Pad009]
  Origin = -> Origin009
  Tip = -> Pad009
FEATURE [Sketcher::SketchObject] Sketch010
  ArcFitTolerance = 0
  AttachmentSupport = -> [XY_Plane009]
  FullyConstrained = true
  MakeInternals = false
  MapMode = 5
  sketch-geometry (13):
    g0: LineSegment StartX=-4.25 StartY=3.75 StartZ=0 EndX=-4.25 EndY=9.25 EndZ=0
    g1: LineSegment StartX=4.25 StartY=3.75 StartZ=0 EndX=4.25 EndY=9.25 EndZ=0
    g2: LineSegment StartX=-4.25 StartY=-3.75 StartZ=0 EndX=-4.25 EndY=-9.25 EndZ=0
    g3: LineSegment StartX=4.25 StartY=-3.75 StartZ=0 EndX=4.25 EndY=-9.25 EndZ=0
    g4: LineSegment StartX=-4.25 StartY=9.25 StartZ=0 EndX=-2.65 EndY=17.2924 EndZ=0
    g5: LineSegment StartX=2.65 StartY=17.2924 StartZ=0 EndX=4.25 EndY=9.25 EndZ=0
    g6: LineSegment StartX=-4.25 StartY=-9.25 StartZ=0 EndX=-2.65 EndY=-17.2924 EndZ=0
    g7: LineSegment StartX=2.65 StartY=-17.2924 StartZ=0 EndX=4.25 EndY=-9.25 EndZ=0
    g8: GeomPoint [constr] X=0 Y=20 Z=0
    g9: ArcOfCircle CenterX=-1e-16 CenterY=17.3494 CenterZ=0 NormalX=0 NormalY=0 NormalZ=1 AngleXU=0 Radius=2.65061 StartAngle=6.26168 EndAngle=9.44628
    g10: ArcOfCircle CenterX=0.0427264 CenterY=-1e-16 CenterZ=0 NormalX=0 NormalY=0 NormalZ=1 AngleXU=0 Radius=5.7 StartAngle=2.42357 EndAngle=3.85961
    g11: ArcOfCircle CenterX=-0.0427264 CenterY=0 CenterZ=0 NormalX=0 NormalY=0 NormalZ=1 AngleXU=0 Radius=5.7 StartAngle=5.56517 EndAngle=7.00121
    g12: ArcOfCircle CenterX=2e-16 CenterY=-17.3494 CenterZ=0 NormalX=0 NormalY=0 NormalZ=1 AngleXU=0 Radius=2.65061 StartAngle=3.12009 EndAngle=6.30469
  constraints (36):
    c: Vertical(g0)
    c: Vertical(g1)
    c: Vertical(g2)
    c: Vertical(g3)
    c: Symmetric(g0,g1,g-2)
    c: Symmetric(g0,g2,g-1)
    c: Symmetric(g2,g3,g-2)
    c: Equal(g1,g0)
    c: Equal(g2,g3)
    c: Equal(g2,g0)
    c: Coincident(g4,g0)
    c: Coincident(g5,g1)
    c: Coincident(g6,g2)
    c: Coincident(g7,g3)
    c: Symmetric(g4,g5,g-2)
    c: Symmetric(g6,g7,g-2)
    c: Symmetric(g4,g6,g-1)
    c: DistanceY(g0,g0) = 5.5
    c: PointOnObject(g8,g-2)
    c: DistanceY(g-1,g8) = 20
    c: Coincident(g9,g4)
    c: Coincident(g9,g5)
    c: Distance(g4) = 8.2
    c: Coincident(g10,g0)
    c: Coincident(g10,g2)
    c: Coincident(g11,g1)
    c: Coincident(g11,g3)
    c: Coincident(g12,g6)
    c: Coincident(g12,g7)
    c: PointOnObject(g8,g9)
    c: DistanceX(g4,g5) = 5.3
    c: Symmetric(g9,g12,g-1)
    c: DistanceY(g2,g0) = 7.5
    c: DistanceX(g0,g1) = 8.5
    c: Radius(g11) = 5.7
    c: Equal(g10,g11)
FEATURE [PartDesign::Pad] Pad010
  Direction = (0,0,1)
  Length = 5
  Length2 = 10
  Profile = -> Sketch010
  ReferenceAxis = -> Sketch010 [N_Axis]
  Suppressed = false
  Type = 0
FEATURE [PartDesign::Body] Body010  label="Lever002"
  AllowCompound = false
  Group = -> [Sketch010,Pad010]
  Origin = -> Origin010
  Placement = pos=(10.5,-10,48) rot=(0,0,1;0rad)
  Tip = -> Pad010
FEATURE [Part::MultiFuse] Fusion024
  Shapes = -> [Body010,Cylinder029]
FEATURE [Part::Cut] Cut014
  Base = -> Body009
  Tool = -> Fusion024
FEATURE [Part::Cut] Cut015  label="Agarre001"
  Base = -> Cut014
  Tool = -> Cylinder030
FEATURE [Part::Box] Box006  label="Cube006"
  AttacherType = Attacher::AttachEngine3D
  Height = 7
  Length = 10
  Placement = pos=(5,-29,7) rot=(0,0,1;0rad)
  Width = 10
FEATURE [Part::Cylinder] Cylinder031
  Angle = 360
  AttacherType = Attacher::AttachEngine3D
  FirstAngle = 0
  Height = 10
  Placement = pos=(10.5,-10.1,-7) rot=(0,0,1;0rad)
  Radius = 3
  SecondAngle = 0
  expr: Radius = Spreadsheet.H_RadioEje
FEATURE [Part::Cylinder] Cylinder032
  Angle = 360
  AttacherType = Attacher::AttachEngine3D
  FirstAngle = 0
  Height = 10
  Placement = pos=(9.9,0,0) rot=(0,0,1;0rad)
  Radius = 0.95
  SecondAngle = 0
  expr: .Placement.Base.x = Spreadsheet.H_RadioTornillos * 2 + Spreadsheet.H_DistanciaTornillos
  expr: Radius = Spreadsheet.H_RadioTornillos
FEATURE [Part::Cylinder] Cylinder033
  Angle = 360
  AttacherType = Attacher::AttachEngine3D
  FirstAngle = 0
  Height = 10
  Radius = 0.95
  SecondAngle = 0
  expr: Radius = Spreadsheet.H_RadioTornillos
FEATURE [Part::Cylinder] Cylinder034
  Angle = 360
  AttacherType = Attacher::AttachEngine3D
  FirstAngle = 0
  Height = 10
  Placement = pos=(9.9,0,0) rot=(0,0,1;0rad)
  Radius = 0.95
  SecondAngle = 0
  expr: .Placement.Base.x = Spreadsheet.H_RadioTornillos * 2 + Spreadsheet.H_DistanciaTornillos
  expr: Radius = Spreadsheet.H_RadioTornillos
FEATURE [Part::Cylinder] Cylinder035
  Angle = 360
  AttacherType = Attacher::AttachEngine3D
  FirstAngle = 0
  Height = 10
  Radius = 0.95
  SecondAngle = 0
  expr: Radius = Spreadsheet.H_RadioTornillos
FEATURE [Part::MultiFuse] Fusion025  label="Tornillos012"
  Placement = pos=(5,24.5,22) rot=(0,0,1;0rad)
  Shapes = -> [Cylinder033,Cylinder032]
FEATURE [Part::MultiFuse] Fusion026  label="Tornillos013"
  Placement = pos=(5,-24.5,22) rot=(0,0,1;0rad)
  Shapes = -> [Cylinder035,Cylinder034]
FEATURE [Part::MultiFuse] Fusion027
  Placement = pos=(0.4,0,0) rot=(0,0,1;0rad)
  Shapes = -> [Fusion025,Fusion026]
FEATURE [Sketcher::SketchObject] Sketch011
  ArcFitTolerance = 0
  AttachmentSupport = -> [YZ_Plane011]
  FullyConstrained = true
  MakeInternals = false
  MapMode = 5
  Placement = pos=(0,0,0) rot=(0.57735,0.57735,0.57735;2.0944rad)
  expr: Constraints[10] = Spreadsheet.H_Largo
  expr: Constraints[12] = Spreadsheet.H_BaseAlto
  expr: Constraints[13] = Spreadsheet.H_AltoServo
  expr: Constraints[14] = Spreadsheet.H_AnchoAgg
  sketch-geometry (8):
    g0: LineSegment StartX=-28.75 StartY=32 StartZ=0 EndX=-28.75 EndY=0 EndZ=0
    g1: LineSegment StartX=-28.75 StartY=0 StartZ=0 EndX=28.75 EndY=0 EndZ=0
    g2: LineSegment StartX=28.75 StartY=0 StartZ=0 EndX=28.75 EndY=32 EndZ=0
    g3: LineSegment StartX=28.75 StartY=32 StartZ=0 EndX=20.75 EndY=32 EndZ=0
    g4: LineSegment StartX=20.75 StartY=32 StartZ=0 EndX=20.75 EndY=3.5 EndZ=0
    g5: LineSegment StartX=20.75 StartY=3.5 StartZ=0 EndX=-20.75 EndY=3.5 EndZ=0
    g6: LineSegment StartX=-20.75 StartY=3.5 StartZ=0 EndX=-20.75 EndY=32 EndZ=0
    g7: LineSegment StartX=-28.75 StartY=32 StartZ=0 EndX=-20.75 EndY=32 EndZ=0
  constraints (21):
    c: Coincident(g1,g0)
    c: Coincident(g2,g1)
    c: Vertical(g2)
    c: Coincident(g3,g2)
    c: Coincident(g4,g3)
    c: Vertical(g4)
    c: Coincident(g5,g4)
    c: Horizontal(g5)
    c: Coincident(g6,g5)
    c: Vertical(g6)
    c: DistanceX(g5,g5) = 41.5
    c: Symmetric(g6,g3,g-2)
    c: DistanceY(g0,g5) = 3.5
    c: DistanceY(g4,g4) = 28.5
    c: DistanceX(g3,g3) = 8
    c: Symmetric(g1,g0,g-2)
    c: Symmetric(g0,g2,g-2)
    c: Coincident(g7,g0)
    c: Coincident(g7,g6)
    c: Horizontal(g7)
    c: PointOnObject(g0,g-1)
FEATURE [PartDesign::Pad] Pad011
  Direction = (1,-2e-16,3e-16)
  Length = 21
  Length2 = 10
  Placement = pos=(0,0,0) rot=(0.57735,0.57735,0.57735;2.0944rad)
  Profile = -> Sketch011
  ReferenceAxis = -> Sketch011 [N_Axis]
  Suppressed = false
  Type = 0
  expr: Length = Spreadsheet.H_AnchoBase
FEATURE [PartDesign::Body] Body011  label="ServoHolder006"
  AllowCompound = false
  Group = -> [Sketch011,Pad011]
  Origin = -> Origin011
  Tip = -> Pad011
FEATURE [Part::Cut] Cut016
  Base = -> Body011
  Tool = -> Box006
FEATURE [Part::Cut] Cut017  label="Holder007"
  Base = -> Cut016
  Tool = -> Fusion027
FEATURE [Part::MultiFuse] Fusion028  label="HolderCEje003"
  Placement = pos=(0,-66,0) rot=(0,0,1;0rad)
  Shapes = -> [Cylinder031,Cut017]
FEATURE [Part::MultiFuse] Fusion029
  Shapes = -> [Fusion028,Cut015]
FEATURE [Part::Cylinder] Cylinder036
  Angle = 360
  AttacherType = Attacher::AttachEngine3D
  FirstAngle = 0
  Height = 9
  Placement = pos=(10.5,-10.1,44) rot=(0,0,1;0rad)
  Radius = 5
  SecondAngle = 0
  expr: Radius = 5
FEATURE [Part::Cylinder] Cylinder037
  Angle = 360
  AttacherType = Attacher::AttachEngine3D
  FirstAngle = 0
  Height = 44
  Placement = pos=(10.5,-10.1,-9) rot=(0,0,1;0rad)
  Radius = 3.4
  SecondAngle = 0
  expr: Radius = Spreadsheet.H_RadioEje + 0.4
FEATURE [Sketcher::SketchObject] Sketch012
  ArcFitTolerance = 0
  AttachmentSupport = -> [YZ_Plane012]
  FullyConstrained = true
  MakeInternals = false
  MapMode = 5
  Placement = pos=(0,0,0) rot=(0.57735,0.57735,0.57735;2.0944rad)
  expr: Constraints[16] = Spreadsheet.U_sepa
  expr: Constraints[17] = Spreadsheet.U_LargoM
  expr: Constraints[20] = Spreadsheet.U_Grosor
  expr: Constraints[21] = Spreadsheet.U_Grosor
  expr: Constraints[22] = Spreadsheet.U_Grosor
  expr: Constraints[23] = Spreadsheet.U_AltoB
  sketch-geometry (8):
    g0: LineSegment StartX=-33 StartY=-0.5 StartZ=0 EndX=0 EndY=-0.5 EndZ=0
    g1: LineSegment StartX=0 StartY=-0.5 StartZ=0 EndX=0 EndY=-5.5 EndZ=0
    g2: LineSegment StartX=0 StartY=-5.5 StartZ=0 EndX=-38 EndY=-5.5 EndZ=0
    g3: LineSegment StartX=-38 StartY=-5.5 StartZ=0 EndX=-38 EndY=50.5 EndZ=0
    g4: LineSegment StartX=-38 StartY=50.5 StartZ=0 EndX=0 EndY=50.5 EndZ=0
    g5: LineSegment StartX=0 StartY=50.5 StartZ=0 EndX=0 EndY=45.5 EndZ=0
    g6: LineSegment StartX=0 StartY=45.5 StartZ=0 EndX=-33 EndY=45.5 EndZ=0
    g7: LineSegment StartX=-33 StartY=45.5 StartZ=0 EndX=-33 EndY=-0.5 EndZ=0
  constraints (24):
    c: Horizontal(g0)
    c: Coincident(g1,g0)
    c: Vertical(g1)
    c: Coincident(g2,g1)
    c: Horizontal(g2)
    c: Coincident(g3,g2)
    c: Vertical(g3)
    c: Coincident(g4,g3)
    c: Horizontal(g4)
    c: Coincident(g5,g4)
    c: Vertical(g5)
    c: Coincident(g6,g5)
    c: Horizontal(g6)
    c: Coincident(g7,g6)
    c: Coincident(g7,g0)
    c: Vertical(g7)
    c: DistanceY(g0,g-1) = 0.5
    c: DistanceX(g0,g-1) = 33
    c: PointOnObject(g0,g-2)
    c: PointOnObject(g5,g-2)
    c: DistanceX(g3,g6) = 5
    c: DistanceY(g5,g4) = 5
    c: DistanceY(g1,g1) = 5
    c: DistanceY(g-1,g5) = 45.5
FEATURE [PartDesign::Pad] Pad012
  Direction = (1,-2e-16,3e-16)
  Length = 21
  Length2 = 10
  Placement = pos=(0,0,0) rot=(0.57735,0.57735,0.57735;2.0944rad)
  Profile = -> Sketch012
  ReferenceAxis = -> Sketch012 [N_Axis]
  Suppressed = false
  Type = 0
  expr: Length = Spreadsheet.H_AnchoBase
FEATURE [PartDesign::Body] Body012  label="U002"
  AllowCompound = false
  Group = -> [Sketch012,Pad012]
  Origin = -> Origin012
  Tip = -> Pad012
FEATURE [Sketcher::SketchObject] Sketch013
  ArcFitTolerance = 0
  AttachmentSupport = -> [XY_Plane012]
  FullyConstrained = true
  MakeInternals = false
  MapMode = 5
  sketch-geometry (13):
    g0: LineSegment StartX=-4.25 StartY=3.75 StartZ=0 EndX=-4.25 EndY=9.25 EndZ=0
    g1: LineSegment StartX=4.25 StartY=3.75 StartZ=0 EndX=4.25 EndY=9.25 EndZ=0
    g2: LineSegment StartX=-4.25 StartY=-3.75 StartZ=0 EndX=-4.25 EndY=-9.25 EndZ=0
    g3: LineSegment StartX=4.25 StartY=-3.75 StartZ=0 EndX=4.25 EndY=-9.25 EndZ=0
    g4: LineSegment StartX=-4.25 StartY=9.25 StartZ=0 EndX=-2.65 EndY=17.2924 EndZ=0
    g5: LineSegment StartX=2.65 StartY=17.2924 StartZ=0 EndX=4.25 EndY=9.25 EndZ=0
    g6: LineSegment StartX=-4.25 StartY=-9.25 StartZ=0 EndX=-2.65 EndY=-17.2924 EndZ=0
    g7: LineSegment StartX=2.65 StartY=-17.2924 StartZ=0 EndX=4.25 EndY=-9.25 EndZ=0
    g8: GeomPoint [constr] X=0 Y=20 Z=0
    g9: ArcOfCircle CenterX=-1e-16 CenterY=17.3494 CenterZ=0 NormalX=0 NormalY=0 NormalZ=1 AngleXU=0 Radius=2.65061 StartAngle=6.26168 EndAngle=9.44628
    g10: ArcOfCircle CenterX=0.0427264 CenterY=-1e-16 CenterZ=0 NormalX=0 NormalY=0 NormalZ=1 AngleXU=0 Radius=5.7 StartAngle=2.42357 EndAngle=3.85961
    g11: ArcOfCircle CenterX=-0.0427264 CenterY=0 CenterZ=0 NormalX=0 NormalY=0 NormalZ=1 AngleXU=0 Radius=5.7 StartAngle=5.56517 EndAngle=7.00121
    g12: ArcOfCircle CenterX=2e-16 CenterY=-17.3494 CenterZ=0 NormalX=0 NormalY=0 NormalZ=1 AngleXU=0 Radius=2.65061 StartAngle=3.12009 EndAngle=6.30469
  constraints (36):
    c: Vertical(g0)
    c: Vertical(g1)
    c: Vertical(g2)
    c: Vertical(g3)
    c: Symmetric(g0,g1,g-2)
    c: Symmetric(g0,g2,g-1)
    c: Symmetric(g2,g3,g-2)
    c: Equal(g1,g0)
    c: Equal(g2,g3)
    c: Equal(g2,g0)
    c: Coincident(g4,g0)
    c: Coincident(g5,g1)
    c: Coincident(g6,g2)
    c: Coincident(g7,g3)
    c: Symmetric(g4,g5,g-2)
    c: Symmetric(g6,g7,g-2)
    c: Symmetric(g4,g6,g-1)
    c: DistanceY(g0,g0) = 5.5
    c: PointOnObject(g8,g-2)
    c: DistanceY(g-1,g8) = 20
    c: Coincident(g9,g4)
    c: Coincident(g9,g5)
    c: Distance(g4) = 8.2
    c: Coincident(g10,g0)
    c: Coincident(g10,g2)
    c: Coincident(g11,g1)
    c: Coincident(g11,g3)
    c: Coincident(g12,g6)
    c: Coincident(g12,g7)
    c: PointOnObject(g8,g9)
    c: DistanceX(g4,g5) = 5.3
    c: Symmetric(g9,g12,g-1)
    c: DistanceY(g2,g0) = 7.5
    c: DistanceX(g0,g1) = 8.5
    c: Radius(g11) = 5.7
    c: Equal(g10,g11)
FEATURE [PartDesign::Pad] Pad013
  Direction = (0,0,1)
  Length = 5
  Length2 = 10
  Profile = -> Sketch013
  ReferenceAxis = -> Sketch013 [N_Axis]
  Suppressed = false
  Type = 0
FEATURE [PartDesign::Body] Body013  label="Lever003"
  AllowCompound = false
  Group = -> [Sketch013,Pad013]
  Origin = -> Origin013
  Placement = pos=(10.5,-10,48) rot=(0,0,1;0rad)
  Tip = -> Pad013
FEATURE [Part::MultiFuse] Fusion030
  Shapes = -> [Body013,Cylinder036]
FEATURE [Part::Cut] Cut018
  Base = -> Body012
  Tool = -> Fusion030
FEATURE [Part::Cut] Cut019  label="Agarre002"
  Base = -> Cut018
  Tool = -> Cylinder037
FEATURE [Part::Cylinder] Cylinder038
  Angle = 360
  AttacherType = Attacher::AttachEngine3D
  FirstAngle = 0
  Height = 9
  Placement = pos=(10.5,-10.1,44) rot=(0,0,1;0rad)
  Radius = 5
  SecondAngle = 0
  expr: Radius = 5
FEATURE [Part::Cylinder] Cylinder039
  Angle = 360
  AttacherType = Attacher::AttachEngine3D
  FirstAngle = 0
  Height = 44
  Placement = pos=(10.5,-10.1,-9) rot=(0,0,1;0rad)
  Radius = 3.4
  SecondAngle = 0
  expr: Radius = Spreadsheet.H_RadioEje + 0.4
FEATURE [Sketcher::SketchObject] Sketch014
  ArcFitTolerance = 0
  AttachmentSupport = -> [YZ_Plane014]
  FullyConstrained = true
  MakeInternals = false
  MapMode = 5
  Placement = pos=(0,0,0) rot=(0.57735,0.57735,0.57735;2.0944rad)
  expr: Constraints[16] = Spreadsheet.U_sepa
  expr: Constraints[17] = Spreadsheet.U_LargoM
  expr: Constraints[20] = Spreadsheet.U_Grosor
  expr: Constraints[21] = Spreadsheet.U_Grosor
  expr: Constraints[22] = Spreadsheet.U_Grosor
  expr: Constraints[23] = Spreadsheet.U_AltoB
  sketch-geometry (8):
    g0: LineSegment StartX=-33 StartY=-0.5 StartZ=0 EndX=0 EndY=-0.5 EndZ=0
    g1: LineSegment StartX=0 StartY=-0.5 StartZ=0 EndX=0 EndY=-5.5 EndZ=0
    g2: LineSegment StartX=0 StartY=-5.5 StartZ=0 EndX=-38 EndY=-5.5 EndZ=0
    g3: LineSegment StartX=-38 StartY=-5.5 StartZ=0 EndX=-38 EndY=50.5 EndZ=0
    g4: LineSegment StartX=-38 StartY=50.5 StartZ=0 EndX=0 EndY=50.5 EndZ=0
    g5: LineSegment StartX=0 StartY=50.5 StartZ=0 EndX=0 EndY=45.5 EndZ=0
    g6: LineSegment StartX=0 StartY=45.5 StartZ=0 EndX=-33 EndY=45.5 EndZ=0
    g7: LineSegment StartX=-33 StartY=45.5 StartZ=0 EndX=-33 EndY=-0.5 EndZ=0
  constraints (24):
    c: Horizontal(g0)
    c: Coincident(g1,g0)
    c: Vertical(g1)
    c: Coincident(g2,g1)
    c: Horizontal(g2)
    c: Coincident(g3,g2)
    c: Vertical(g3)
    c: Coincident(g4,g3)
    c: Horizontal(g4)
    c: Coincident(g5,g4)
    c: Vertical(g5)
    c: Coincident(g6,g5)
    c: Horizontal(g6)
    c: Coincident(g7,g6)
    c: Coincident(g7,g0)
    c: Vertical(g7)
    c: DistanceY(g0,g-1) = 0.5
    c: DistanceX(g0,g-1) = 33
    c: PointOnObject(g0,g-2)
    c: PointOnObject(g5,g-2)
    c: DistanceX(g3,g6) = 5
    c: DistanceY(g5,g4) = 5
    c: DistanceY(g1,g1) = 5
    c: DistanceY(g-1,g5) = 45.5
FEATURE [PartDesign::Pad] Pad014
  Direction = (1,-2e-16,3e-16)
  Length = 21
  Length2 = 10
  Placement = pos=(0,0,0) rot=(0.57735,0.57735,0.57735;2.0944rad)
  Profile = -> Sketch014
  ReferenceAxis = -> Sketch014 [N_Axis]
  Suppressed = false
  Type = 0
  expr: Length = Spreadsheet.H_AnchoBase
FEATURE [PartDesign::Body] Body014  label="U003"
  AllowCompound = false
  Group = -> [Sketch014,Pad014]
  Origin = -> Origin014
  Tip = -> Pad014
FEATURE [Sketcher::SketchObject] Sketch015
  ArcFitTolerance = 0
  AttachmentSupport = -> [XY_Plane014]
  FullyConstrained = true
  MakeInternals = false
  MapMode = 5
  sketch-geometry (13):
    g0: LineSegment StartX=-4.25 StartY=3.75 StartZ=0 EndX=-4.25 EndY=9.25 EndZ=0
    g1: LineSegment StartX=4.25 StartY=3.75 StartZ=0 EndX=4.25 EndY=9.25 EndZ=0
    g2: LineSegment StartX=-4.25 StartY=-3.75 StartZ=0 EndX=-4.25 EndY=-9.25 EndZ=0
    g3: LineSegment StartX=4.25 StartY=-3.75 StartZ=0 EndX=4.25 EndY=-9.25 EndZ=0
    g4: LineSegment StartX=-4.25 StartY=9.25 StartZ=0 EndX=-2.65 EndY=17.2924 EndZ=0
    g5: LineSegment StartX=2.65 StartY=17.2924 StartZ=0 EndX=4.25 EndY=9.25 EndZ=0
    g6: LineSegment StartX=-4.25 StartY=-9.25 StartZ=0 EndX=-2.65 EndY=-17.2924 EndZ=0
    g7: LineSegment StartX=2.65 StartY=-17.2924 StartZ=0 EndX=4.25 EndY=-9.25 EndZ=0
    g8: GeomPoint [constr] X=0 Y=20 Z=0
    g9: ArcOfCircle CenterX=-1e-16 CenterY=17.3494 CenterZ=0 NormalX=0 NormalY=0 NormalZ=1 AngleXU=0 Radius=2.65061 StartAngle=6.26168 EndAngle=9.44628
    g10: ArcOfCircle CenterX=0.0427264 CenterY=-1e-16 CenterZ=0 NormalX=0 NormalY=0 NormalZ=1 AngleXU=0 Radius=5.7 StartAngle=2.42357 EndAngle=3.85961
    g11: ArcOfCircle CenterX=-0.0427264 CenterY=0 CenterZ=0 NormalX=0 NormalY=0 NormalZ=1 AngleXU=0 Radius=5.7 StartAngle=5.56517 EndAngle=7.00121
    g12: ArcOfCircle CenterX=2e-16 CenterY=-17.3494 CenterZ=0 NormalX=0 NormalY=0 NormalZ=1 AngleXU=0 Radius=2.65061 StartAngle=3.12009 EndAngle=6.30469
  constraints (36):
    c: Vertical(g0)
    c: Vertical(g1)
    c: Vertical(g2)
    c: Vertical(g3)
    c: Symmetric(g0,g1,g-2)
    c: Symmetric(g0,g2,g-1)
    c: Symmetric(g2,g3,g-2)
    c: Equal(g1,g0)
    c: Equal(g2,g3)
    c: Equal(g2,g0)
    c: Coincident(g4,g0)
    c: Coincident(g5,g1)
    c: Coincident(g6,g2)
    c: Coincident(g7,g3)
    c: Symmetric(g4,g5,g-2)
    c: Symmetric(g6,g7,g-2)
    c: Symmetric(g4,g6,g-1)
    c: DistanceY(g0,g0) = 5.5
    c: PointOnObject(g8,g-2)
    c: DistanceY(g-1,g8) = 20
    c: Coincident(g9,g4)
    c: Coincident(g9,g5)
    c: Distance(g4) = 8.2
    c: Coincident(g10,g0)
    c: Coincident(g10,g2)
    c: Coincident(g11,g1)
    c: Coincident(g11,g3)
    c: Coincident(g12,g6)
    c: Coincident(g12,g7)
    c: PointOnObject(g8,g9)
    c: DistanceX(g4,g5) = 5.3
    c: Symmetric(g9,g12,g-1)
    c: DistanceY(g2,g0) = 7.5
    c: DistanceX(g0,g1) = 8.5
    c: Radius(g11) = 5.7
    c: Equal(g10,g11)
FEATURE [PartDesign::Pad] Pad015
  Direction = (0,0,1)
  Length = 5
  Length2 = 10
  Profile = -> Sketch015
  ReferenceAxis = -> Sketch015 [N_Axis]
  Suppressed = false
  Type = 0
FEATURE [PartDesign::Body] Body015  label="Lever004"
  AllowCompound = false
  Group = -> [Sketch015,Pad015]
  Origin = -> Origin015
  Placement = pos=(10.5,-10,48) rot=(0,0,1;0rad)
  Tip = -> Pad015
FEATURE [Part::MultiFuse] Fusion031
  Shapes = -> [Body015,Cylinder038]
FEATURE [Part::Cut] Cut020
  Base = -> Body014
  Tool = -> Fusion031
FEATURE [Part::Cut] Cut021  label="Agarre003"
  Base = -> Cut020
  Placement = pos=(32,-71,32) rot=(0.707107,0,-0.707107;3.14159rad)
  Tool = -> Cylinder039
FEATURE [Part::MultiFuse] Fusion032  label="Cadera"
  Shapes = -> [Cut019,Cut021]
FEATURE [App::DocumentObjectGroup] Group003  label="Agarres"
  Group = -> [Fusion029,Fusion032]
FEATURE [Part::Box] Box007  label="Cube007"
  AttacherType = Attacher::AttachEngine3D
  Height = 7
  Length = 10
  Placement = pos=(5,-29,7) rot=(0,0,1;0rad)
  Width = 10
FEATURE [Part::Box] Box008  label="Cube008"
  AttacherType = Attacher::AttachEngine3D
  Height = 7
  Length = 10
  Placement = pos=(5,-29,7) rot=(0,0,1;0rad)
  Width = 10
FEATURE [Part::Cylinder] Cylinder040
  Angle = 360
  AttacherType = Attacher::AttachEngine3D
  FirstAngle = 0
  Height = 10
  Placement = pos=(10.5,-10.1,-7) rot=(0,0,1;0rad)
  Radius = 3
  SecondAngle = 0
  expr: Radius = Spreadsheet.H_RadioEje
FEATURE [Part::Cylinder] Cylinder041
  Angle = 360
  AttacherType = Attacher::AttachEngine3D
  FirstAngle = 0
  Height = 10
  Placement = pos=(9.9,0,0) rot=(0,0,1;0rad)
  Radius = 0.95
  SecondAngle = 0
  expr: .Placement.Base.x = Spreadsheet.H_RadioTornillos * 2 + Spreadsheet.H_DistanciaTornillos
  expr: Radius = Spreadsheet.H_RadioTornillos
FEATURE [Part::Cylinder] Cylinder042
  Angle = 360
  AttacherType = Attacher::AttachEngine3D
  FirstAngle = 0
  Height = 10
  Radius = 0.95
  SecondAngle = 0
  expr: Radius = Spreadsheet.H_RadioTornillos
FEATURE [Part::Cylinder] Cylinder043
  Angle = 360
  AttacherType = Attacher::AttachEngine3D
  FirstAngle = 0
  Height = 10
  Placement = pos=(9.9,0,0) rot=(0,0,1;0rad)
  Radius = 0.95
  SecondAngle = 0
  expr: .Placement.Base.x = Spreadsheet.H_RadioTornillos * 2 + Spreadsheet.H_DistanciaTornillos
  expr: Radius = Spreadsheet.H_RadioTornillos
FEATURE [Part::Cylinder] Cylinder044
  Angle = 360
  AttacherType = Attacher::AttachEngine3D
  FirstAngle = 0
  Height = 10
  Radius = 0.95
  SecondAngle = 0
  expr: Radius = Spreadsheet.H_RadioTornillos
FEATURE [Part::Cylinder] Cylinder045
  Angle = 360
  AttacherType = Attacher::AttachEngine3D
  FirstAngle = 0
  Height = 10
  Placement = pos=(10.5,-10.1,-7) rot=(0,0,1;0rad)
  Radius = 3
  SecondAngle = 0
  expr: Radius = Spreadsheet.H_RadioEje
FEATURE [Part::Cylinder] Cylinder046
  Angle = 360
  AttacherType = Attacher::AttachEngine3D
  FirstAngle = 0
  Height = 10
  Placement = pos=(9.9,0,0) rot=(0,0,1;0rad)
  Radius = 0.95
  SecondAngle = 0
  expr: .Placement.Base.x = Spreadsheet.H_RadioTornillos * 2 + Spreadsheet.H_DistanciaTornillos
  expr: Radius = Spreadsheet.H_RadioTornillos
FEATURE [Part::Cylinder] Cylinder047
  Angle = 360
  AttacherType = Attacher::AttachEngine3D
  FirstAngle = 0
  Height = 10
  Radius = 0.95
  SecondAngle = 0
  expr: Radius = Spreadsheet.H_RadioTornillos
FEATURE [Part::Cylinder] Cylinder048
  Angle = 360
  AttacherType = Attacher::AttachEngine3D
  FirstAngle = 0
  Height = 10
  Placement = pos=(9.9,0,0) rot=(0,0,1;0rad)
  Radius = 0.95
  SecondAngle = 0
  expr: .Placement.Base.x = Spreadsheet.H_RadioTornillos * 2 + Spreadsheet.H_DistanciaTornillos
  expr: Radius = Spreadsheet.H_RadioTornillos
FEATURE [Part::Cylinder] Cylinder049
  Angle = 360
  AttacherType = Attacher::AttachEngine3D
  FirstAngle = 0
  Height = 10
  Radius = 0.95
  SecondAngle = 0
  expr: Radius = Spreadsheet.H_RadioTornillos
FEATURE [Part::MultiFuse] Fusion033  label="Tornillos014"
  Placement = pos=(5,24.5,22) rot=(0,0,1;0rad)
  Shapes = -> [Cylinder042,Cylinder041]
FEATURE [Part::MultiFuse] Fusion034  label="Tornillos015"
  Placement = pos=(5,-24.5,22) rot=(0,0,1;0rad)
  Shapes = -> [Cylinder044,Cylinder043]
FEATURE [Part::MultiFuse] Fusion035
  Placement = pos=(0.4,0,0) rot=(0,0,1;0rad)
  Shapes = -> [Fusion033,Fusion034]
FEATURE [Part::MultiFuse] Fusion037  label="Tornillos016"
  Placement = pos=(5,24.5,22) rot=(0,0,1;0rad)
  Shapes = -> [Cylinder047,Cylinder046]
FEATURE [Part::MultiFuse] Fusion038  label="Tornillos017"
  Placement = pos=(5,-24.5,22) rot=(0,0,1;0rad)
  Shapes = -> [Cylinder049,Cylinder048]
FEATURE [Part::MultiFuse] Fusion039
  Placement = pos=(0.4,0,0) rot=(0,0,1;0rad)
  Shapes = -> [Fusion037,Fusion038]
FEATURE [Sketcher::SketchObject] Sketch016
  ArcFitTolerance = 0
  AttachmentSupport = -> [YZ_Plane016]
  FullyConstrained = true
  MakeInternals = false
  MapMode = 5
  Placement = pos=(0,0,0) rot=(0.57735,0.57735,0.57735;2.0944rad)
  expr: Constraints[10] = Spreadsheet.H_Largo
  expr: Constraints[12] = Spreadsheet.H_BaseAlto
  expr: Constraints[13] = Spreadsheet.H_AltoServo
  expr: Constraints[14] = Spreadsheet.H_AnchoAgg
  sketch-geometry (8):
    g0: LineSegment StartX=-28.75 StartY=32 StartZ=0 EndX=-28.75 EndY=0 EndZ=0
    g1: LineSegment StartX=-28.75 StartY=0 StartZ=0 EndX=28.75 EndY=0 EndZ=0
    g2: LineSegment StartX=28.75 StartY=0 StartZ=0 EndX=28.75 EndY=32 EndZ=0
    g3: LineSegment StartX=28.75 StartY=32 StartZ=0 EndX=20.75 EndY=32 EndZ=0
    g4: LineSegment StartX=20.75 StartY=32 StartZ=0 EndX=20.75 EndY=3.5 EndZ=0
    g5: LineSegment StartX=20.75 StartY=3.5 StartZ=0 EndX=-20.75 EndY=3.5 EndZ=0
    g6: LineSegment StartX=-20.75 StartY=3.5 StartZ=0 EndX=-20.75 EndY=32 EndZ=0
    g7: LineSegment StartX=-28.75 StartY=32 StartZ=0 EndX=-20.75 EndY=32 EndZ=0
  constraints (21):
    c: Coincident(g1,g0)
    c: Coincident(g2,g1)
    c: Vertical(g2)
    c: Coincident(g3,g2)
    c: Coincident(g4,g3)
    c: Vertical(g4)
    c: Coincident(g5,g4)
    c: Horizontal(g5)
    c: Coincident(g6,g5)
    c: Vertical(g6)
    c: DistanceX(g5,g5) = 41.5
    c: Symmetric(g6,g3,g-2)
    c: DistanceY(g0,g5) = 3.5
    c: DistanceY(g4,g4) = 28.5
    c: DistanceX(g3,g3) = 8
    c: Symmetric(g1,g0,g-2)
    c: Symmetric(g0,g2,g-2)
    c: Coincident(g7,g0)
    c: Coincident(g7,g6)
    c: Horizontal(g7)
    c: PointOnObject(g0,g-1)
FEATURE [PartDesign::Pad] Pad016
  Direction = (1,-2e-16,3e-16)
  Length = 21
  Length2 = 10
  Placement = pos=(0,0,0) rot=(0.57735,0.57735,0.57735;2.0944rad)
  Profile = -> Sketch016
  ReferenceAxis = -> Sketch016 [N_Axis]
  Suppressed = false
  Type = 0
  expr: Length = Spreadsheet.H_AnchoBase
FEATURE [PartDesign::Body] Body016  label="ServoHolder007"
  AllowCompound = false
  Group = -> [Sketch016,Pad016]
  Origin = -> Origin016
  Tip = -> Pad016
FEATURE [Part::Cut] Cut022
  Base = -> Body016
  Tool = -> Box007
FEATURE [Part::Cut] Cut023  label="Holder008"
  Base = -> Cut022
  Tool = -> Fusion035
FEATURE [Part::MultiFuse] Fusion036  label="HolderCEje004"
  Shapes = -> [Cylinder040,Cut023]
FEATURE [Sketcher::SketchObject] Sketch017
  ArcFitTolerance = 0
  AttachmentSupport = -> [YZ_Plane017]
  FullyConstrained = true
  MakeInternals = false
  MapMode = 5
  Placement = pos=(0,0,0) rot=(0.57735,0.57735,0.57735;2.0944rad)
  expr: Constraints[10] = Spreadsheet.H_Largo
  expr: Constraints[12] = Spreadsheet.H_BaseAlto
  expr: Constraints[13] = Spreadsheet.H_AltoServo
  expr: Constraints[14] = Spreadsheet.H_AnchoAgg
  sketch-geometry (8):
    g0: LineSegment StartX=-28.75 StartY=32 StartZ=0 EndX=-28.75 EndY=0 EndZ=0
    g1: LineSegment StartX=-28.75 StartY=0 StartZ=0 EndX=28.75 EndY=0 EndZ=0
    g2: LineSegment StartX=28.75 StartY=0 StartZ=0 EndX=28.75 EndY=32 EndZ=0
    g3: LineSegment StartX=28.75 StartY=32 StartZ=0 EndX=20.75 EndY=32 EndZ=0
    g4: LineSegment StartX=20.75 StartY=32 StartZ=0 EndX=20.75 EndY=3.5 EndZ=0
    g5: LineSegment StartX=20.75 StartY=3.5 StartZ=0 EndX=-20.75 EndY=3.5 EndZ=0
    g6: LineSegment StartX=-20.75 StartY=3.5 StartZ=0 EndX=-20.75 EndY=32 EndZ=0
    g7: LineSegment StartX=-28.75 StartY=32 StartZ=0 EndX=-20.75 EndY=32 EndZ=0
  constraints (21):
    c: Coincident(g1,g0)
    c: Coincident(g2,g1)
    c: Vertical(g2)
    c: Coincident(g3,g2)
    c: Coincident(g4,g3)
    c: Vertical(g4)
    c: Coincident(g5,g4)
    c: Horizontal(g5)
    c: Coincident(g6,g5)
    c: Vertical(g6)
    c: DistanceX(g5,g5) = 41.5
    c: Symmetric(g6,g3,g-2)
    c: DistanceY(g0,g5) = 3.5
    c: DistanceY(g4,g4) = 28.5
    c: DistanceX(g3,g3) = 8
    c: Symmetric(g1,g0,g-2)
    c: Symmetric(g0,g2,g-2)
    c: Coincident(g7,g0)
    c: Coincident(g7,g6)
    c: Horizontal(g7)
    c: PointOnObject(g0,g-1)
FEATURE [PartDesign::Pad] Pad017
  Direction = (1,-2e-16,3e-16)
  Length = 21
  Length2 = 10
  Placement = pos=(0,0,0) rot=(0.57735,0.57735,0.57735;2.0944rad)
  Profile = -> Sketch017
  ReferenceAxis = -> Sketch017 [N_Axis]
  Suppressed = false
  Type = 0
  expr: Length = Spreadsheet.H_AnchoBase
FEATURE [PartDesign::Body] Body017  label="ServoHolder008"
  AllowCompound = false
  Group = -> [Sketch017,Pad017]
  Origin = -> Origin017
  Tip = -> Pad017
FEATURE [Part::Cut] Cut024
  Base = -> Body017
  Tool = -> Box008
FEATURE [Part::Cut] Cut025  label="Holder009"
  Base = -> Cut024
  Tool = -> Fusion039
FEATURE [Part::MultiFuse] Fusion040  label="HolderCEje005"
  Placement = pos=(21,57,0) rot=(0,0,1;3.14159rad)
  Shapes = -> [Cylinder045,Cut025]
FEATURE [Part::MultiFuse] Fusion041  label="Cadera001"
  Shapes = -> [Fusion040,Fusion036]
FEATURE [Part::Cylinder] Cylinder050
  Angle = 360
  AttacherType = Attacher::AttachEngine3D
  FirstAngle = 0
  Height = 7
  Placement = pos=(7,28.5,25) rot=(0,-1,0;1.5708rad)
  Radius = 0.9
  SecondAngle = 0
FEATURE [Part::Cylinder] Cylinder051
  Angle = 360
  AttacherType = Attacher::AttachEngine3D
  FirstAngle = 0
  Height = 7
  Placement = pos=(7,28.5,5) rot=(0,-1,0;1.5708rad)
  Radius = 0.9
  SecondAngle = 0
FEATURE [Part::MultiFuse] Fusion042
  Shapes = -> [Cylinder051,Cylinder050]
FEATURE [Part::Cut] Cut026
  Base = -> Fusion041
  Tool = -> Fusion042
FEATURE [App::DocumentObjectGroup] Group005  label="Group"
  Group = -> [Cut026]
FEATURE [Part::Cylinder] Cylinder052
  Angle = 360
  AttacherType = Attacher::AttachEngine3D
  FirstAngle = 0
  Height = 9
  Placement = pos=(10.5,-10.1,44) rot=(0,0,1;0rad)
  Radius = 5
  SecondAngle = 0
  expr: Radius = 5
FEATURE [Part::Cylinder] Cylinder053
  Angle = 360
  AttacherType = Attacher::AttachEngine3D
  FirstAngle = 0
  Height = 44
  Placement = pos=(10.5,-10.1,-9) rot=(0,0,1;0rad)
  Radius = 3.4
  SecondAngle = 0
  expr: Radius = Spreadsheet.H_RadioEje + 0.4
FEATURE [Sketcher::SketchObject] Sketch018
  ArcFitTolerance = 0
  AttachmentSupport = -> [YZ_Plane018]
  FullyConstrained = true
  MakeInternals = false
  MapMode = 5
  Placement = pos=(0,0,0) rot=(0.57735,0.57735,0.57735;2.0944rad)
  expr: Constraints[16] = Spreadsheet.U_sepa
  expr: Constraints[17] = Spreadsheet.U_LargoM
  expr: Constraints[20] = Spreadsheet.U_Grosor
  expr: Constraints[21] = Spreadsheet.U_Grosor
  expr: Constraints[22] = Spreadsheet.U_Grosor
  expr: Constraints[23] = Spreadsheet.U_AltoB
  sketch-geometry (8):
    g0: LineSegment StartX=-33 StartY=-0.5 StartZ=0 EndX=0 EndY=-0.5 EndZ=0
    g1: LineSegment StartX=0 StartY=-0.5 StartZ=0 EndX=0 EndY=-5.5 EndZ=0
    g2: LineSegment StartX=0 StartY=-5.5 StartZ=0 EndX=-38 EndY=-5.5 EndZ=0
    g3: LineSegment StartX=-38 StartY=-5.5 StartZ=0 EndX=-38 EndY=50.5 EndZ=0
    g4: LineSegment StartX=-38 StartY=50.5 StartZ=0 EndX=0 EndY=50.5 EndZ=0
    g5: LineSegment StartX=0 StartY=50.5 StartZ=0 EndX=0 EndY=45.5 EndZ=0
    g6: LineSegment StartX=0 StartY=45.5 StartZ=0 EndX=-33 EndY=45.5 EndZ=0
    g7: LineSegment StartX=-33 StartY=45.5 StartZ=0 EndX=-33 EndY=-0.5 EndZ=0
  constraints (24):
    c: Horizontal(g0)
    c: Coincident(g1,g0)
    c: Vertical(g1)
    c: Coincident(g2,g1)
    c: Horizontal(g2)
    c: Coincident(g3,g2)
    c: Vertical(g3)
    c: Coincident(g4,g3)
    c: Horizontal(g4)
    c: Coincident(g5,g4)
    c: Vertical(g5)
    c: Coincident(g6,g5)
    c: Horizontal(g6)
    c: Coincident(g7,g6)
    c: Coincident(g7,g0)
    c: Vertical(g7)
    c: DistanceY(g0,g-1) = 0.5
    c: DistanceX(g0,g-1) = 33
    c: PointOnObject(g0,g-2)
    c: PointOnObject(g5,g-2)
    c: DistanceX(g3,g6) = 5
    c: DistanceY(g5,g4) = 5
    c: DistanceY(g1,g1) = 5
    c: DistanceY(g-1,g5) = 45.5
FEATURE [PartDesign::Pad] Pad018
  Direction = (1,-2e-16,3e-16)
  Length = 21
  Length2 = 10
  Placement = pos=(0,0,0) rot=(0.57735,0.57735,0.57735;2.0944rad)
  Profile = -> Sketch018
  ReferenceAxis = -> Sketch018 [N_Axis]
  Suppressed = false
  Type = 0
  expr: Length = Spreadsheet.H_AnchoBase
FEATURE [PartDesign::Body] Body018  label="U004"
  AllowCompound = false
  Group = -> [Sketch018,Pad018]
  Origin = -> Origin018
  Tip = -> Pad018
FEATURE [Sketcher::SketchObject] Sketch019
  ArcFitTolerance = 0
  AttachmentSupport = -> [XY_Plane018]
  FullyConstrained = true
  MakeInternals = false
  MapMode = 5
  sketch-geometry (13):
    g0: LineSegment StartX=-4.25 StartY=3.75 StartZ=0 EndX=-4.25 EndY=9.25 EndZ=0
    g1: LineSegment StartX=4.25 StartY=3.75 StartZ=0 EndX=4.25 EndY=9.25 EndZ=0
    g2: LineSegment StartX=-4.25 StartY=-3.75 StartZ=0 EndX=-4.25 EndY=-9.25 EndZ=0
    g3: LineSegment StartX=4.25 StartY=-3.75 StartZ=0 EndX=4.25 EndY=-9.25 EndZ=0
    g4: LineSegment StartX=-4.25 StartY=9.25 StartZ=0 EndX=-2.65 EndY=17.2924 EndZ=0
    g5: LineSegment StartX=2.65 StartY=17.2924 StartZ=0 EndX=4.25 EndY=9.25 EndZ=0
    g6: LineSegment StartX=-4.25 StartY=-9.25 StartZ=0 EndX=-2.65 EndY=-17.2924 EndZ=0
    g7: LineSegment StartX=2.65 StartY=-17.2924 StartZ=0 EndX=4.25 EndY=-9.25 EndZ=0
    g8: GeomPoint [constr] X=0 Y=20 Z=0
    g9: ArcOfCircle CenterX=-1e-16 CenterY=17.3494 CenterZ=0 NormalX=0 NormalY=0 NormalZ=1 AngleXU=0 Radius=2.65061 StartAngle=6.26168 EndAngle=9.44628
    g10: ArcOfCircle CenterX=0.0427264 CenterY=-1e-16 CenterZ=0 NormalX=0 NormalY=0 NormalZ=1 AngleXU=0 Radius=5.7 StartAngle=2.42357 EndAngle=3.85961
    g11: ArcOfCircle CenterX=-0.0427264 CenterY=0 CenterZ=0 NormalX=0 NormalY=0 NormalZ=1 AngleXU=0 Radius=5.7 StartAngle=5.56517 EndAngle=7.00121
    g12: ArcOfCircle CenterX=2e-16 CenterY=-17.3494 CenterZ=0 NormalX=0 NormalY=0 NormalZ=1 AngleXU=0 Radius=2.65061 StartAngle=3.12009 EndAngle=6.30469
  constraints (36):
    c: Vertical(g0)
    c: Vertical(g1)
    c: Vertical(g2)
    c: Vertical(g3)
    c: Symmetric(g0,g1,g-2)
    c: Symmetric(g0,g2,g-1)
    c: Symmetric(g2,g3,g-2)
    c: Equal(g1,g0)
    c: Equal(g2,g3)
    c: Equal(g2,g0)
    c: Coincident(g4,g0)
    c: Coincident(g5,g1)
    c: Coincident(g6,g2)
    c: Coincident(g7,g3)
    c: Symmetric(g4,g5,g-2)
    c: Symmetric(g6,g7,g-2)
    c: Symmetric(g4,g6,g-1)
    c: DistanceY(g0,g0) = 5.5
    c: PointOnObject(g8,g-2)
    c: DistanceY(g-1,g8) = 20
    c: Coincident(g9,g4)
    c: Coincident(g9,g5)
    c: Distance(g4) = 8.2
    c: Coincident(g10,g0)
    c: Coincident(g10,g2)
    c: Coincident(g11,g1)
    c: Coincident(g11,g3)
    c: Coincident(g12,g6)
    c: Coincident(g12,g7)
    c: PointOnObject(g8,g9)
    c: DistanceX(g4,g5) = 5.3
    c: Symmetric(g9,g12,g-1)
    c: DistanceY(g2,g0) = 7.5
    c: DistanceX(g0,g1) = 8.5
    c: Radius(g11) = 5.7
    c: Equal(g10,g11)
FEATURE [PartDesign::Pad] Pad019
  Direction = (0,0,1)
  Length = 5
  Length2 = 10
  Profile = -> Sketch019
  ReferenceAxis = -> Sketch019 [N_Axis]
  Suppressed = false
  Type = 0
FEATURE [PartDesign::Body] Body019  label="Lever005"
  AllowCompound = false
  Group = -> [Sketch019,Pad019]
  Origin = -> Origin019
  Placement = pos=(10.5,-10,48) rot=(0,0,1;0rad)
  Tip = -> Pad019
FEATURE [Part::MultiFuse] Fusion043
  Shapes = -> [Body019,Cylinder052]
FEATURE [Part::Cut] Cut027
  Base = -> Body018
  Tool = -> Fusion043
FEATURE [Part::Cut] Cut028  label="Agarre004"
  Base = -> Cut027
  Placement = pos=(0,0,0) rot=(1,0,0;1.5708rad)
  Tool = -> Cylinder053
FEATURE [Sketcher::SketchObject] Sketch020
  ArcFitTolerance = 0
  AttachmentSupport = -> [XY_Plane019]
  FullyConstrained = false
  MakeInternals = false
  MapMode = 5
  expr: Constraints[8] = Spreadsheet.P_acnho
  expr: Constraints[9] = Spreadsheet.P_largo
  sketch-geometry (4):
    g0: LineSegment StartX=-6.9511 StartY=8.37276 StartZ=0 EndX=-6.9511 EndY=-53.6272 EndZ=0
    g1: LineSegment StartX=-6.9511 StartY=-53.6272 StartZ=0 EndX=28.0489 EndY=-53.6272 EndZ=0
    g2: LineSegment StartX=28.0489 StartY=-53.6272 StartZ=0 EndX=28.0489 EndY=8.37276 EndZ=0
    g3: LineSegment StartX=28.0489 StartY=8.37276 StartZ=0 EndX=-6.9511 EndY=8.37276 EndZ=0
  constraints (10):
    c: Vertical(g0)
    c: Coincident(g1,g0)
    c: Horizontal(g1)
    c: Coincident(g2,g1)
    c: Vertical(g2)
    c: Coincident(g3,g2)
    c: Coincident(g3,g0)
    c: Horizontal(g3)
    c: DistanceX(g3,g3) = 35
    c: DistanceY(g2,g2) = 62
FEATURE [PartDesign::Pad] Pad020
  Direction = (0,0,1)
  Length = 3
  Length2 = 10
  Profile = -> Sketch020
  ReferenceAxis = -> Sketch020 [N_Axis]
  Suppressed = false
  Type = 0
FEATURE [PartDesign::Body] Body020  label="Body"
  AllowCompound = false
  Group = -> [Sketch020,Pad020]
  Origin = -> Origin020
  Placement = pos=(0,0,-39) rot=(0,0,1;0rad)
  Tip = -> Pad020
FEATURE [Part::MultiFuse] Fusion044
  Shapes = -> [Body020,Cut028]
FEATURE [App::DocumentObjectGroup] Group006  label="foot"
  Group = -> [Fusion044]
FEATURE [Sketcher::SketchObject] Sketch021
  ArcFitTolerance = 0
  AttachmentSupport = -> [XY_Plane020]
  FullyConstrained = true
  MakeInternals = false
  MapMode = 5
  sketch-geometry (13):
    g0: LineSegment StartX=-4.25 StartY=3.75 StartZ=0 EndX=-4.25 EndY=9.25 EndZ=0
    g1: LineSegment StartX=4.25 StartY=3.75 StartZ=0 EndX=4.25 EndY=9.25 EndZ=0
    g2: LineSegment StartX=-4.25 StartY=-3.75 StartZ=0 EndX=-4.25 EndY=-9.25 EndZ=0
    g3: LineSegment StartX=4.25 StartY=-3.75 StartZ=0 EndX=4.25 EndY=-9.25 EndZ=0
    g4: LineSegment StartX=-4.25 StartY=9.25 StartZ=0 EndX=-2.65 EndY=17.2924 EndZ=0
    g5: LineSegment StartX=2.65 StartY=17.2924 StartZ=0 EndX=4.25 EndY=9.25 EndZ=0
    g6: LineSegment StartX=-4.25 StartY=-9.25 StartZ=0 EndX=-2.65 EndY=-17.2924 EndZ=0
    g7: LineSegment StartX=2.65 StartY=-17.2924 StartZ=0 EndX=4.25 EndY=-9.25 EndZ=0
    g8: GeomPoint [constr] X=0 Y=20 Z=0
    g9: ArcOfCircle CenterX=-1e-16 CenterY=17.3494 CenterZ=0 NormalX=0 NormalY=0 NormalZ=1 AngleXU=0 Radius=2.65061 StartAngle=6.26168 EndAngle=9.44628
    g10: ArcOfCircle CenterX=0.0427264 CenterY=-1e-16 CenterZ=0 NormalX=0 NormalY=0 NormalZ=1 AngleXU=0 Radius=5.7 StartAngle=2.42357 EndAngle=3.85961
    g11: ArcOfCircle CenterX=-0.0427264 CenterY=0 CenterZ=0 NormalX=0 NormalY=0 NormalZ=1 AngleXU=0 Radius=5.7 StartAngle=5.56517 EndAngle=7.00121
    g12: ArcOfCircle CenterX=2e-16 CenterY=-17.3494 CenterZ=0 NormalX=0 NormalY=0 NormalZ=1 AngleXU=0 Radius=2.65061 StartAngle=3.12009 EndAngle=6.30469
  constraints (36):
    c: Vertical(g0)
    c: Vertical(g1)
    c: Vertical(g2)
    c: Vertical(g3)
    c: Symmetric(g0,g1,g-2)
    c: Symmetric(g0,g2,g-1)
    c: Symmetric(g2,g3,g-2)
    c: Equal(g1,g0)
    c: Equal(g2,g3)
    c: Equal(g2,g0)
    c: Coincident(g4,g0)
    c: Coincident(g5,g1)
    c: Coincident(g6,g2)
    c: Coincident(g7,g3)
    c: Symmetric(g4,g5,g-2)
    c: Symmetric(g6,g7,g-2)
    c: Symmetric(g4,g6,g-1)
    c: DistanceY(g0,g0) = 5.5
    c: PointOnObject(g8,g-2)
    c: DistanceY(g-1,g8) = 20
    c: Coincident(g9,g4)
    c: Coincident(g9,g5)
    c: Distance(g4) = 8.2
    c: Coincident(g10,g0)
    c: Coincident(g10,g2)
    c: Coincident(g11,g1)
    c: Coincident(g11,g3)
    c: Coincident(g12,g6)
    c: Coincident(g12,g7)
    c: PointOnObject(g8,g9)
    c: DistanceX(g4,g5) = 5.3
    c: Symmetric(g9,g12,g-1)
    c: DistanceY(g2,g0) = 7.5
    c: DistanceX(g0,g1) = 8.5
    c: Radius(g11) = 5.7
    c: Equal(g10,g11)
FEATURE [PartDesign::Pad] Pad021
  Direction = (0,0,1)
  Length = 5
  Length2 = 10
  Profile = -> Sketch021
  ReferenceAxis = -> Sketch021 [N_Axis]
  Suppressed = false
  Type = 0
FEATURE [PartDesign::Body] Body021  label="Lever006"
  AllowCompound = false
  Group = -> [Sketch021,Pad021]
  Origin = -> Origin021
  Placement = pos=(25,29,18) rot=(0,-1,0;1.5708rad)
  Tip = -> Pad021
FEATURE [Part::Box] Box011  label="Cube011"
  AttacherType = Attacher::AttachEngine3D
  Height = 32
  Length = 4
  Placement = pos=(21,-28.5,0) rot=(0,0,1;0rad)
  Width = 114
FEATURE [Sketcher::SketchObject] Sketch022
  ArcFitTolerance = 0
  AttachmentSupport = -> [XY_Plane021]
  FullyConstrained = false
  MakeInternals = false
  MapMode = 5
  sketch-geometry (3):
    g0: GeomPoint [constr] X=0 Y=20 Z=0
    g1: ArcOfCircle CenterX=0.042726 CenterY=0 CenterZ=0 NormalX=0 NormalY=0 NormalZ=1 AngleXU=0 Radius=5.7 StartAngle=1.57829 EndAngle=4.70489
    g2: ArcOfCircle CenterX=-0.042726 CenterY=0 CenterZ=0 NormalX=0 NormalY=0 NormalZ=1 AngleXU=0 Radius=5.7 StartAngle=4.71988 EndAngle=7.84649
  constraints (9):
    c: PointOnObject(g0,g-2)
    c: Radius(g2) = 5.7
    c: DistanceX(g2) = -0.042726
    c: DistanceY(g2) = 0
    c: DistanceX(g1) = 0.042726
    c: DistanceY(g1) = 0
    c: Radius(g1) = 5.7
    c: Coincident(g2,g1)
    c: Coincident(g2,g1)
FEATURE [PartDesign::Pad] Pad022
  Direction = (0,0,1)
  Length = 10
  Length2 = 10
  Profile = -> Sketch022
  ReferenceAxis = -> Sketch022 [N_Axis]
  Suppressed = false
  Type = 0
FEATURE [PartDesign::Body] Body022  label="Lever007"
  AllowCompound = false
  Group = -> [Sketch022,Pad022]
  Origin = -> Origin022
  Placement = pos=(31,29,18) rot=(0,-1,0;1.5708rad)
  Tip = -> Pad022
FEATURE [Part::Box] Box012  label="Cube012"
  AttacherType = Attacher::AttachEngine3D
  Height = 32
  Length = 3
  Placement = pos=(23.5,-28.5,0) rot=(0,0,1;0rad)
  Width = 114
FEATURE [Part::Cut] Cut029
  Base = -> Box012
  Tool = -> Body022
FEATURE [Part::Cut] Cut030
  Base = -> Box011
  Placement = pos=(-1,0,0) rot=(0,0,1;0rad)
  Tool = -> Body021
FEATURE [Part::MultiFuse] Fusion045
  Shapes = -> [Cut030,Cut029]
FEATURE [App::DocumentObjectGroup] Group007  label="Cintura"
  Group = -> [Fusion045]
